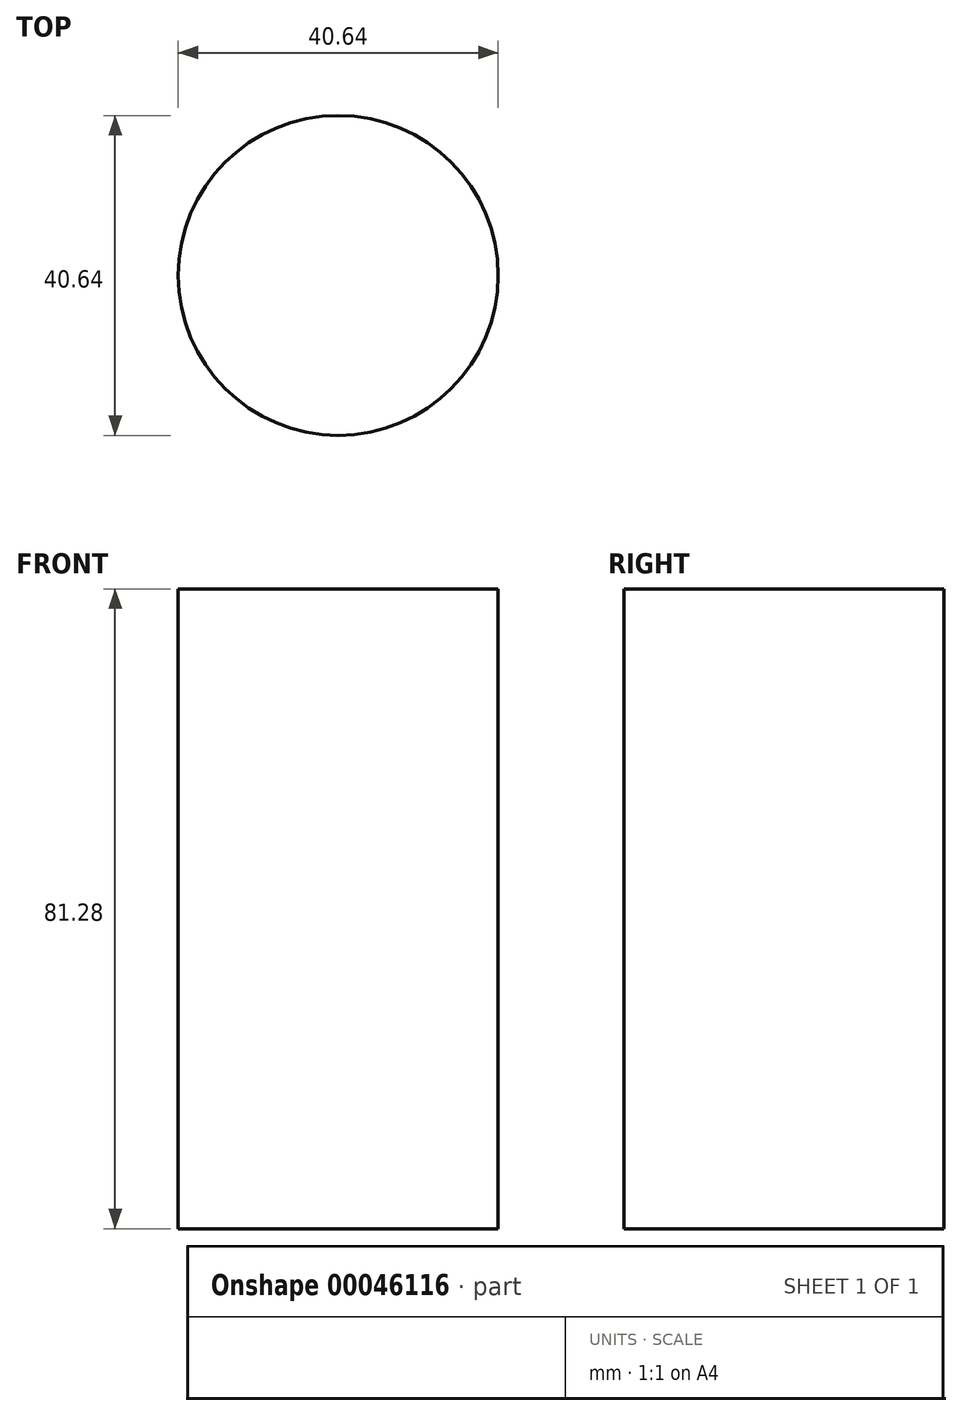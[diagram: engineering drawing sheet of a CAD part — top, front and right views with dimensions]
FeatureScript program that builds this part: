
annotation { "Feature Type Name" : "Feature", "Feature Type Description" : "" }
export const myFeature = defineFeature(function(context is Context, id is Id, definition is map)
    precondition{}
    {
        {
            var Q0;
            Q0=qCreatedBy(makeId("Top.planeOp"),FACE);
            var sketch = newSketch(context, id + "F0", { "sketchPlane" : qUnion([Q0])});
            skCircle(sketch, "E0", {"center": v(0, 0) * mm, "radius": 20.32 * mm});
            skSolve(sketch);
        }
        {
            var Q0;
            Q0 = qSketchRegion(id + "F0", true);
            extrude(context, id + "F1", {"entities" : qUnion([Q0]), "depth" : 81.28 * mm, "offsetDistance" : 25.4 * mm});
        }
        {
            var Q0;
            Q0=qCreatedBy(makeId("Front.planeOp"),FACE);
            var sketch = newSketch(context, id + "F2", { "sketchPlane" : qUnion([Q0])});
            skFitSpline(sketch, "E1", {"points": [v(-16.9, 70.92) * mm, v(-19.25, 69.07) * mm, v(-21.18, 67.72) * mm, v(-23.18, 66.68) * mm, v(-25, 65.87) * mm, v(-27.08, 65.45) * mm, v(-28.89, 65.52) * mm, v(-31.24, 66.18) * mm, v(-33.28, 67.14) * mm, v(-35.6, 68.65) * mm, v(-37.98, 70.46) * mm, v(-40.6, 72.58) * mm, v(-43.3, 74.85) * mm, v(-45.92, 76.97) * mm, v(-47.77, 78.27) * mm, v(-49.55, 79.34) * mm, v(-51.69, 80.25) * mm, v(-52.99, 80.6) * mm, v(-54.31, 80.8) * mm, v(-56.45, 80.67) * mm, v(-58.72, 79.96) * mm, v(-61.18, 78.63) * mm, v(-63.97, 76.63) * mm, v(-65.94, 74.93) * mm, v(-68.23, 72.96) * mm, v(-70.75, 70.8) * mm, v(-72.95, 68.98) * mm, v(-74.77, 67.65) * mm, v(-76.5, 66.54) * mm, v(-78.4, 65.67) * mm, v(-79.9, 65.25) * mm], "startDerivative": vector(-65.6, -51.95) * mm, "endDerivative": vector(-54.28, -13.22) * mm});
            skLineSegment(sketch, "E2", {"start": v(-16.9, 70.92) * mm, "end": v(-16.9, 68.66) * mm});
            skFitSpline(sketch, "E3", {"points": [v(-16.9, 68.66) * mm, v(-18.1, 67.65) * mm, v(-19.82, 66.42) * mm, v(-21.63, 65.25) * mm, v(-23.53, 64.2) * mm, v(-25.25, 63.55) * mm, v(-27.13, 63.23) * mm, v(-29.05, 63.26) * mm, v(-31.45, 64) * mm, v(-34.55, 65.71) * mm, v(-37.5, 67.72) * mm, v(-39.84, 69.69) * mm, v(-42.44, 71.83) * mm, v(-44.25, 73.34) * mm, v(-46.14, 74.8) * mm, v(-47.72, 75.94) * mm, v(-49.32, 76.96) * mm, v(-51.05, 77.73) * mm, v(-52.82, 78.3) * mm, v(-55.16, 78.56) * mm, v(-57.51, 78.17) * mm, v(-60.32, 76.79) * mm, v(-63.06, 74.94) * mm, v(-65.76, 72.85) * mm, v(-67.49, 71.27) * mm, v(-70.66, 68.66) * mm, v(-72.37, 67.09) * mm, v(-74.17, 65.8) * mm, v(-75.98, 64.66) * mm, v(-77.76, 63.73) * mm, v(-79.9, 62.91) * mm], "startDerivative": vector(-42.76, -36.86) * mm, "endDerivative": vector(-68.1, -24.19) * mm});
            skLineSegment(sketch, "E4", {"start": v(-79.9, 65.25) * mm, "end": v(-79.9, 62.91) * mm});
            skFitSpline(sketch, "E5", {"points": [v(-16.9, 74.77) * mm, v(-19.25, 72.92) * mm, v(-21.18, 71.57) * mm, v(-23.18, 70.53) * mm, v(-25, 69.72) * mm, v(-27.08, 69.3) * mm, v(-28.89, 69.37) * mm, v(-31.24, 70.03) * mm, v(-33.28, 71) * mm, v(-35.6, 72.5) * mm, v(-37.98, 74.3) * mm, v(-40.6, 76.43) * mm, v(-43.3, 78.7) * mm, v(-45.92, 80.82) * mm, v(-47.77, 82.12) * mm, v(-49.55, 83.19) * mm, v(-51.69, 84.1) * mm, v(-52.99, 84.45) * mm, v(-54.31, 84.65) * mm, v(-56.45, 84.52) * mm, v(-58.72, 83.8) * mm, v(-61.18, 82.48) * mm, v(-63.97, 80.48) * mm, v(-65.94, 78.78) * mm, v(-68.23, 76.81) * mm, v(-70.75, 74.66) * mm, v(-72.95, 72.82) * mm, v(-74.77, 71.5) * mm, v(-76.5, 70.4) * mm, v(-78.4, 69.52) * mm, v(-79.9, 69.1) * mm], "startDerivative": vector(-65.6, -51.95) * mm, "endDerivative": vector(-54.28, -13.22) * mm});
            skLineSegment(sketch, "E6", {"start": v(-16.9, 74.77) * mm, "end": v(-16.9, 72.51) * mm});
            skFitSpline(sketch, "E7", {"points": [v(-16.9, 72.51) * mm, v(-18.1, 71.5) * mm, v(-19.82, 70.27) * mm, v(-21.63, 69.1) * mm, v(-23.53, 68.04) * mm, v(-25.25, 67.4) * mm, v(-27.13, 67.08) * mm, v(-29.05, 67.1) * mm, v(-31.45, 67.84) * mm, v(-34.55, 69.56) * mm, v(-37.5, 71.57) * mm, v(-39.84, 73.54) * mm, v(-42.44, 75.68) * mm, v(-44.25, 77.18) * mm, v(-46.14, 78.65) * mm, v(-47.72, 79.79) * mm, v(-49.32, 80.8) * mm, v(-51.05, 81.58) * mm, v(-52.82, 82.16) * mm, v(-55.16, 82.4) * mm, v(-57.51, 82.02) * mm, v(-60.32, 80.63) * mm, v(-63.06, 78.78) * mm, v(-65.76, 76.7) * mm, v(-67.49, 75.12) * mm, v(-70.66, 72.51) * mm, v(-72.37, 70.94) * mm, v(-74.17, 69.65) * mm, v(-75.98, 68.5) * mm, v(-77.76, 67.58) * mm, v(-79.9, 66.76) * mm], "startDerivative": vector(-42.76, -36.86) * mm, "endDerivative": vector(-68.1, -24.19) * mm});
            skLineSegment(sketch, "E8", {"start": v(-79.9, 69.1) * mm, "end": v(-79.9, 66.76) * mm});
            skFitSpline(sketch, "E9", {"points": [v(-16.9, 78.33) * mm, v(-19.25, 76.47) * mm, v(-21.18, 75.12) * mm, v(-23.18, 74.08) * mm, v(-25, 73.27) * mm, v(-27.08, 72.85) * mm, v(-28.89, 72.93) * mm, v(-31.24, 73.58) * mm, v(-33.28, 74.55) * mm, v(-35.6, 76.05) * mm, v(-37.98, 77.86) * mm, v(-40.6, 79.98) * mm, v(-43.3, 82.25) * mm, v(-45.92, 84.38) * mm, v(-47.77, 85.67) * mm, v(-49.55, 86.74) * mm, v(-51.69, 87.65) * mm, v(-52.99, 88) * mm, v(-54.31, 88.2) * mm, v(-56.45, 88.07) * mm, v(-58.72, 87.36) * mm, v(-61.18, 86.03) * mm, v(-63.97, 84.03) * mm, v(-65.94, 82.34) * mm, v(-68.23, 80.37) * mm, v(-70.75, 78.21) * mm, v(-72.95, 76.38) * mm, v(-74.77, 75.05) * mm, v(-76.5, 73.95) * mm, v(-78.4, 73.07) * mm, v(-79.9, 72.65) * mm], "startDerivative": vector(-65.6, -51.95) * mm, "endDerivative": vector(-54.28, -13.22) * mm});
            skLineSegment(sketch, "E10", {"start": v(-16.9, 78.33) * mm, "end": v(-16.9, 76.07) * mm});
            skFitSpline(sketch, "E11", {"points": [v(-16.9, 76.07) * mm, v(-18.1, 75.06) * mm, v(-19.82, 73.82) * mm, v(-21.63, 72.65) * mm, v(-23.53, 71.6) * mm, v(-25.25, 70.96) * mm, v(-27.13, 70.64) * mm, v(-29.05, 70.66) * mm, v(-31.45, 71.4) * mm, v(-34.55, 73.11) * mm, v(-37.5, 75.12) * mm, v(-39.84, 77.1) * mm, v(-42.44, 79.24) * mm, v(-44.25, 80.74) * mm, v(-46.14, 82.2) * mm, v(-47.72, 83.34) * mm, v(-49.32, 84.36) * mm, v(-51.05, 85.13) * mm, v(-52.82, 85.71) * mm, v(-55.16, 85.96) * mm, v(-57.51, 85.58) * mm, v(-60.32, 84.19) * mm, v(-63.06, 82.34) * mm, v(-65.76, 80.26) * mm, v(-67.49, 78.68) * mm, v(-70.66, 76.07) * mm, v(-72.37, 74.49) * mm, v(-74.17, 73.2) * mm, v(-75.98, 72.06) * mm, v(-77.76, 71.13) * mm, v(-79.9, 70.32) * mm], "startDerivative": vector(-42.76, -36.86) * mm, "endDerivative": vector(-68.1, -24.19) * mm});
            skLineSegment(sketch, "E12", {"start": v(-79.9, 72.65) * mm, "end": v(-79.9, 70.32) * mm});
            skFitSpline(sketch, "E13", {"points": [v(-16.9, 81.98) * mm, v(-19.25, 80.13) * mm, v(-21.18, 78.78) * mm, v(-23.18, 77.74) * mm, v(-25, 76.93) * mm, v(-27.08, 76.5) * mm, v(-28.89, 76.58) * mm, v(-31.24, 77.24) * mm, v(-33.28, 78.2) * mm, v(-35.6, 79.7) * mm, v(-37.98, 81.52) * mm, v(-40.6, 83.64) * mm, v(-43.3, 85.9) * mm, v(-45.92, 88.03) * mm, v(-47.77, 89.33) * mm, v(-49.55, 90.4) * mm, v(-51.69, 91.3) * mm, v(-52.99, 91.66) * mm, v(-54.31, 91.86) * mm, v(-56.45, 91.73) * mm, v(-58.72, 91.01) * mm, v(-61.18, 89.69) * mm, v(-63.97, 87.69) * mm, v(-65.94, 86) * mm, v(-68.23, 84.02) * mm, v(-70.75, 81.87) * mm, v(-72.95, 80.03) * mm, v(-74.77, 78.7) * mm, v(-76.5, 77.6) * mm, v(-78.4, 76.73) * mm, v(-79.9, 76.3) * mm], "startDerivative": vector(-65.6, -51.95) * mm, "endDerivative": vector(-54.28, -13.22) * mm});
            skLineSegment(sketch, "E14", {"start": v(-16.9, 81.71) * mm, "end": v(-16.9, 79.72) * mm});
            skFitSpline(sketch, "E15", {"points": [v(-16.9, 79.72) * mm, v(-18.1, 78.71) * mm, v(-19.82, 77.48) * mm, v(-21.63, 76.3) * mm, v(-23.53, 75.25) * mm, v(-25.25, 74.61) * mm, v(-27.13, 74.3) * mm, v(-29.05, 74.32) * mm, v(-31.45, 75.05) * mm, v(-34.55, 76.77) * mm, v(-37.5, 78.78) * mm, v(-39.84, 80.75) * mm, v(-42.44, 82.9) * mm, v(-44.25, 84.4) * mm, v(-46.14, 85.86) * mm, v(-47.72, 87) * mm, v(-49.32, 88.02) * mm, v(-51.05, 88.79) * mm, v(-52.82, 89.37) * mm, v(-55.16, 89.62) * mm, v(-57.51, 89.23) * mm, v(-60.32, 87.84) * mm, v(-63.06, 86) * mm, v(-65.76, 83.91) * mm, v(-67.49, 82.33) * mm, v(-70.66, 79.72) * mm, v(-72.37, 78.15) * mm, v(-74.17, 76.87) * mm, v(-75.98, 75.72) * mm, v(-77.76, 74.79) * mm, v(-79.9, 73.97) * mm], "startDerivative": vector(-42.76, -36.86) * mm, "endDerivative": vector(-68.1, -24.19) * mm});
            skLineSegment(sketch, "E16", {"start": v(-79.9, 76.3) * mm, "end": v(-79.9, 73.97) * mm});
            skFitSpline(sketch, "E17", {"points": [v(-16.9, 85.8) * mm, v(-19.25, 83.95) * mm, v(-21.18, 82.6) * mm, v(-23.18, 81.56) * mm, v(-25, 80.75) * mm, v(-27.08, 80.33) * mm, v(-28.89, 80.4) * mm, v(-31.24, 81.06) * mm, v(-33.28, 82.03) * mm, v(-35.6, 83.53) * mm, v(-37.98, 85.34) * mm, v(-40.6, 87.46) * mm, v(-43.3, 89.73) * mm, v(-45.92, 91.86) * mm, v(-47.77, 93.15) * mm, v(-49.55, 94.22) * mm, v(-51.69, 95.13) * mm, v(-52.99, 95.49) * mm, v(-54.31, 95.68) * mm, v(-56.45, 95.55) * mm, v(-58.72, 94.84) * mm, v(-61.18, 93.5) * mm, v(-63.97, 91.51) * mm, v(-65.94, 89.82) * mm, v(-68.23, 87.85) * mm, v(-70.75, 85.7) * mm, v(-72.95, 83.86) * mm, v(-74.77, 82.53) * mm, v(-76.5, 81.43) * mm, v(-78.4, 80.55) * mm, v(-79.9, 80.13) * mm], "startDerivative": vector(-65.6, -51.95) * mm, "endDerivative": vector(-54.28, -13.22) * mm});
            skLineSegment(sketch, "E18", {"start": v(-16.9, 85.8) * mm, "end": v(-16.9, 83.55) * mm});
            skFitSpline(sketch, "E19", {"points": [v(-16.9, 83.55) * mm, v(-18.1, 82.54) * mm, v(-19.82, 81.3) * mm, v(-21.63, 80.13) * mm, v(-23.53, 79.08) * mm, v(-25.25, 78.44) * mm, v(-27.13, 78.11) * mm, v(-29.05, 78.14) * mm, v(-31.45, 78.88) * mm, v(-34.55, 80.6) * mm, v(-37.5, 82.6) * mm, v(-39.84, 84.57) * mm, v(-42.44, 86.72) * mm, v(-44.25, 88.22) * mm, v(-46.14, 89.68) * mm, v(-47.72, 90.82) * mm, v(-49.32, 91.84) * mm, v(-51.05, 92.61) * mm, v(-52.82, 93.19) * mm, v(-55.16, 93.44) * mm, v(-57.51, 93.06) * mm, v(-60.32, 91.67) * mm, v(-63.06, 89.82) * mm, v(-65.76, 87.74) * mm, v(-67.49, 86.15) * mm, v(-70.66, 83.55) * mm, v(-72.37, 81.97) * mm, v(-74.17, 80.69) * mm, v(-75.98, 79.54) * mm, v(-77.76, 78.61) * mm, v(-79.9, 77.8) * mm], "startDerivative": vector(-42.76, -36.86) * mm, "endDerivative": vector(-68.1, -24.19) * mm});
            skLineSegment(sketch, "E20", {"start": v(-79.9, 80.13) * mm, "end": v(-79.9, 77.8) * mm});
            skFitSpline(sketch, "E21", {"points": [v(-16.9, 67.25) * mm, v(-19.25, 65.4) * mm, v(-21.18, 64.05) * mm, v(-23.18, 63) * mm, v(-25, 62.2) * mm, v(-27.08, 61.78) * mm, v(-28.89, 61.85) * mm, v(-31.24, 62.5) * mm, v(-33.28, 63.47) * mm, v(-35.6, 64.97) * mm, v(-37.98, 66.79) * mm, v(-40.6, 68.9) * mm, v(-43.3, 71.18) * mm, v(-45.92, 73.3) * mm, v(-47.77, 74.6) * mm, v(-49.55, 75.67) * mm, v(-51.69, 76.58) * mm, v(-52.99, 76.93) * mm, v(-54.31, 77.13) * mm, v(-56.45, 77) * mm, v(-58.72, 76.28) * mm, v(-61.18, 74.96) * mm, v(-63.97, 72.96) * mm, v(-65.94, 71.26) * mm, v(-68.23, 69.3) * mm, v(-70.75, 67.14) * mm, v(-72.95, 65.3) * mm, v(-74.77, 63.97) * mm, v(-76.5, 62.87) * mm, v(-78.4, 62) * mm, v(-79.9, 61.58) * mm], "startDerivative": vector(-65.6, -51.95) * mm, "endDerivative": vector(-54.28, -13.22) * mm});
            skLineSegment(sketch, "E22", {"start": v(-16.9, 67.25) * mm, "end": v(-16.9, 65) * mm});
            skFitSpline(sketch, "E23", {"points": [v(-16.9, 65) * mm, v(-18.1, 63.98) * mm, v(-19.82, 62.75) * mm, v(-21.63, 61.58) * mm, v(-23.53, 60.52) * mm, v(-25.25, 59.88) * mm, v(-27.13, 59.56) * mm, v(-29.05, 59.59) * mm, v(-31.45, 60.32) * mm, v(-34.55, 62.04) * mm, v(-37.5, 64.05) * mm, v(-39.84, 66.02) * mm, v(-42.44, 68.16) * mm, v(-44.25, 69.66) * mm, v(-46.14, 71.13) * mm, v(-47.72, 72.27) * mm, v(-49.32, 73.29) * mm, v(-51.05, 74.06) * mm, v(-52.82, 74.64) * mm, v(-55.16, 74.89) * mm, v(-57.51, 74.5) * mm, v(-60.32, 73.11) * mm, v(-63.06, 71.26) * mm, v(-65.76, 69.18) * mm, v(-67.49, 67.6) * mm, v(-70.66, 65) * mm, v(-72.37, 63.42) * mm, v(-74.17, 62.13) * mm, v(-75.98, 60.98) * mm, v(-77.76, 60.06) * mm, v(-79.9, 59.24) * mm], "startDerivative": vector(-42.76, -36.86) * mm, "endDerivative": vector(-68.1, -24.19) * mm});
            skLineSegment(sketch, "E24", {"start": v(-79.9, 61.58) * mm, "end": v(-79.9, 59.24) * mm});
            skFitSpline(sketch, "E25", {"points": [v(-16.9, 63.52) * mm, v(-19.25, 61.66) * mm, v(-21.18, 60.32) * mm, v(-23.18, 59.28) * mm, v(-25, 58.47) * mm, v(-27.08, 58.04) * mm, v(-28.89, 58.12) * mm, v(-31.24, 58.77) * mm, v(-33.28, 59.74) * mm, v(-35.6, 61.24) * mm, v(-37.98, 63.05) * mm, v(-40.6, 65.17) * mm, v(-43.3, 67.45) * mm, v(-45.92, 69.57) * mm, v(-47.77, 70.87) * mm, v(-49.55, 71.93) * mm, v(-51.69, 72.84) * mm, v(-52.99, 73.2) * mm, v(-54.31, 73.4) * mm, v(-56.45, 73.26) * mm, v(-58.72, 72.55) * mm, v(-61.18, 71.22) * mm, v(-63.97, 69.22) * mm, v(-65.94, 67.53) * mm, v(-68.23, 65.56) * mm, v(-70.75, 63.4) * mm, v(-72.95, 61.57) * mm, v(-74.77, 60.24) * mm, v(-76.5, 59.14) * mm, v(-78.4, 58.26) * mm, v(-79.9, 57.84) * mm], "startDerivative": vector(-65.6, -51.95) * mm, "endDerivative": vector(-54.28, -13.22) * mm});
            skLineSegment(sketch, "E26", {"start": v(-16.9, 63.52) * mm, "end": v(-16.9, 61.26) * mm});
            skFitSpline(sketch, "E27", {"points": [v(-16.9, 61.26) * mm, v(-18.1, 60.25) * mm, v(-19.82, 59.01) * mm, v(-21.63, 57.84) * mm, v(-23.53, 56.79) * mm, v(-25.25, 56.15) * mm, v(-27.13, 55.83) * mm, v(-29.05, 55.85) * mm, v(-31.45, 56.59) * mm, v(-34.55, 58.3) * mm, v(-37.5, 60.32) * mm, v(-39.84, 62.28) * mm, v(-42.44, 64.43) * mm, v(-44.25, 65.93) * mm, v(-46.14, 67.4) * mm, v(-47.72, 68.53) * mm, v(-49.32, 69.55) * mm, v(-51.05, 70.32) * mm, v(-52.82, 70.9) * mm, v(-55.16, 71.15) * mm, v(-57.51, 70.77) * mm, v(-60.32, 69.38) * mm, v(-63.06, 67.53) * mm, v(-65.76, 65.45) * mm, v(-67.49, 63.87) * mm, v(-70.66, 61.26) * mm, v(-72.37, 59.68) * mm, v(-74.17, 58.4) * mm, v(-75.98, 57.25) * mm, v(-77.76, 56.32) * mm, v(-79.9, 55.5) * mm], "startDerivative": vector(-42.76, -36.86) * mm, "endDerivative": vector(-68.1, -24.19) * mm});
            skLineSegment(sketch, "E28", {"start": v(-79.9, 57.84) * mm, "end": v(-79.9, 55.5) * mm});
            skFitSpline(sketch, "E29", {"points": [v(-16.9, 60.09) * mm, v(-19.25, 58.23) * mm, v(-21.18, 56.88) * mm, v(-23.18, 55.84) * mm, v(-25, 55.03) * mm, v(-27.08, 54.6) * mm, v(-28.89, 54.69) * mm, v(-31.24, 55.34) * mm, v(-33.28, 56.3) * mm, v(-35.6, 57.8) * mm, v(-37.98, 59.62) * mm, v(-40.6, 61.74) * mm, v(-43.3, 64.01) * mm, v(-45.92, 66.14) * mm, v(-47.77, 67.43) * mm, v(-49.55, 68.5) * mm, v(-51.69, 69.4) * mm, v(-52.99, 69.77) * mm, v(-54.31, 69.96) * mm, v(-56.45, 69.83) * mm, v(-58.72, 69.12) * mm, v(-61.18, 67.79) * mm, v(-63.97, 65.8) * mm, v(-65.94, 64.1) * mm, v(-68.23, 62.12) * mm, v(-70.75, 59.97) * mm, v(-72.95, 58.14) * mm, v(-74.77, 56.8) * mm, v(-76.5, 55.7) * mm, v(-78.4, 54.83) * mm, v(-79.9, 54.4) * mm], "startDerivative": vector(-65.6, -51.95) * mm, "endDerivative": vector(-54.28, -13.22) * mm});
            skLineSegment(sketch, "E30", {"start": v(-16.9, 60.09) * mm, "end": v(-16.9, 57.82) * mm});
            skFitSpline(sketch, "E31", {"points": [v(-16.9, 57.82) * mm, v(-18.1, 56.82) * mm, v(-19.82, 55.58) * mm, v(-21.63, 54.41) * mm, v(-23.53, 53.36) * mm, v(-25.25, 52.71) * mm, v(-27.13, 52.4) * mm, v(-29.05, 52.42) * mm, v(-31.45, 53.16) * mm, v(-34.55, 54.87) * mm, v(-37.5, 56.88) * mm, v(-39.84, 58.85) * mm, v(-42.44, 61) * mm, v(-44.25, 62.5) * mm, v(-46.14, 63.96) * mm, v(-47.72, 65.1) * mm, v(-49.32, 66.12) * mm, v(-51.05, 66.9) * mm, v(-52.82, 67.47) * mm, v(-55.16, 67.72) * mm, v(-57.51, 67.34) * mm, v(-60.32, 65.95) * mm, v(-63.06, 64.1) * mm, v(-65.76, 62.02) * mm, v(-67.49, 60.43) * mm, v(-70.66, 57.82) * mm, v(-72.37, 56.25) * mm, v(-74.17, 54.97) * mm, v(-75.98, 53.82) * mm, v(-77.76, 52.9) * mm, v(-79.9, 52.07) * mm], "startDerivative": vector(-42.76, -36.86) * mm, "endDerivative": vector(-68.1, -24.19) * mm});
            skLineSegment(sketch, "E32", {"start": v(-79.9, 54.4) * mm, "end": v(-79.9, 52.07) * mm});
            skFitSpline(sketch, "E33", {"points": [v(-16.9, 56.45) * mm, v(-19.25, 54.6) * mm, v(-21.18, 53.25) * mm, v(-23.18, 52.21) * mm, v(-25, 51.4) * mm, v(-27.08, 50.98) * mm, v(-28.89, 51.05) * mm, v(-31.24, 51.7) * mm, v(-33.28, 52.67) * mm, v(-35.6, 54.18) * mm, v(-37.98, 55.99) * mm, v(-40.6, 58.1) * mm, v(-43.3, 60.38) * mm, v(-45.92, 62.5) * mm, v(-47.77, 63.8) * mm, v(-49.55, 64.87) * mm, v(-51.69, 65.78) * mm, v(-52.99, 66.13) * mm, v(-54.31, 66.33) * mm, v(-56.45, 66.2) * mm, v(-58.72, 65.49) * mm, v(-61.18, 64.16) * mm, v(-63.97, 62.16) * mm, v(-65.94, 60.46) * mm, v(-68.23, 58.5) * mm, v(-70.75, 56.34) * mm, v(-72.95, 54.5) * mm, v(-74.77, 53.18) * mm, v(-76.5, 52.07) * mm, v(-78.4, 51.2) * mm, v(-79.9, 50.78) * mm], "startDerivative": vector(-65.6, -51.95) * mm, "endDerivative": vector(-54.28, -13.22) * mm});
            skLineSegment(sketch, "E34", {"start": v(-16.9, 56.45) * mm, "end": v(-16.9, 54.2) * mm});
            skFitSpline(sketch, "E35", {"points": [v(-16.9, 54.2) * mm, v(-18.1, 53.18) * mm, v(-19.82, 51.95) * mm, v(-21.63, 50.78) * mm, v(-23.53, 49.72) * mm, v(-25.25, 49.08) * mm, v(-27.13, 48.76) * mm, v(-29.05, 48.79) * mm, v(-31.45, 49.52) * mm, v(-34.55, 51.24) * mm, v(-37.5, 53.25) * mm, v(-39.84, 55.22) * mm, v(-42.44, 57.36) * mm, v(-44.25, 58.87) * mm, v(-46.14, 60.33) * mm, v(-47.72, 61.47) * mm, v(-49.32, 62.49) * mm, v(-51.05, 63.26) * mm, v(-52.82, 63.84) * mm, v(-55.16, 64.09) * mm, v(-57.51, 63.7) * mm, v(-60.32, 62.32) * mm, v(-63.06, 60.47) * mm, v(-65.76, 58.38) * mm, v(-67.49, 56.8) * mm, v(-70.66, 54.2) * mm, v(-72.37, 52.62) * mm, v(-74.17, 51.34) * mm, v(-75.98, 50.19) * mm, v(-77.76, 49.26) * mm, v(-79.9, 48.44) * mm], "startDerivative": vector(-42.76, -36.86) * mm, "endDerivative": vector(-68.1, -24.19) * mm});
            skLineSegment(sketch, "E36", {"start": v(-79.9, 50.78) * mm, "end": v(-79.9, 48.44) * mm});
            skFitSpline(sketch, "E37", {"points": [v(-16.9, 52.7) * mm, v(-19.25, 50.84) * mm, v(-21.18, 49.5) * mm, v(-23.18, 48.45) * mm, v(-25, 47.64) * mm, v(-27.08, 47.22) * mm, v(-28.89, 47.3) * mm, v(-31.24, 47.95) * mm, v(-33.28, 48.91) * mm, v(-35.6, 50.42) * mm, v(-37.98, 52.23) * mm, v(-40.6, 54.35) * mm, v(-43.3, 56.62) * mm, v(-45.92, 58.74) * mm, v(-47.77, 60.04) * mm, v(-49.55, 61.11) * mm, v(-51.69, 62.02) * mm, v(-52.99, 62.37) * mm, v(-54.31, 62.57) * mm, v(-56.45, 62.44) * mm, v(-58.72, 61.73) * mm, v(-61.18, 60.4) * mm, v(-63.97, 58.4) * mm, v(-65.94, 56.7) * mm, v(-68.23, 54.73) * mm, v(-70.75, 52.58) * mm, v(-72.95, 50.75) * mm, v(-74.77, 49.42) * mm, v(-76.5, 48.31) * mm, v(-78.4, 47.44) * mm, v(-79.9, 47.02) * mm], "startDerivative": vector(-65.6, -51.95) * mm, "endDerivative": vector(-54.28, -13.22) * mm});
            skLineSegment(sketch, "E38", {"start": v(-16.9, 52.7) * mm, "end": v(-16.9, 50.43) * mm});
            skFitSpline(sketch, "E39", {"points": [v(-16.9, 50.43) * mm, v(-18.1, 49.43) * mm, v(-19.82, 48.19) * mm, v(-21.63, 47.02) * mm, v(-23.53, 45.97) * mm, v(-25.25, 45.32) * mm, v(-27.13, 45) * mm, v(-29.05, 45.03) * mm, v(-31.45, 45.76) * mm, v(-34.55, 47.48) * mm, v(-37.5, 49.5) * mm, v(-39.84, 51.46) * mm, v(-42.44, 53.6) * mm, v(-44.25, 55.1) * mm, v(-46.14, 56.57) * mm, v(-47.72, 57.7) * mm, v(-49.32, 58.73) * mm, v(-51.05, 59.5) * mm, v(-52.82, 60.08) * mm, v(-55.16, 60.33) * mm, v(-57.51, 59.94) * mm, v(-60.32, 58.56) * mm, v(-63.06, 56.7) * mm, v(-65.76, 54.63) * mm, v(-67.49, 53.04) * mm, v(-70.66, 50.43) * mm, v(-72.37, 48.86) * mm, v(-74.17, 47.58) * mm, v(-75.98, 46.43) * mm, v(-77.76, 45.5) * mm, v(-79.9, 44.68) * mm], "startDerivative": vector(-42.76, -36.86) * mm, "endDerivative": vector(-68.1, -24.19) * mm});
            skLineSegment(sketch, "E40", {"start": v(-79.9, 47.02) * mm, "end": v(-79.9, 44.68) * mm});
            skFitSpline(sketch, "E41", {"points": [v(-16.9, 49.16) * mm, v(-19.25, 47.3) * mm, v(-21.18, 45.96) * mm, v(-23.18, 44.92) * mm, v(-25, 44.11) * mm, v(-27.08, 43.69) * mm, v(-28.89, 43.76) * mm, v(-31.24, 44.42) * mm, v(-33.28, 45.38) * mm, v(-35.6, 46.89) * mm, v(-37.98, 48.7) * mm, v(-40.6, 50.82) * mm, v(-43.3, 53.1) * mm, v(-45.92, 55.21) * mm, v(-47.77, 56.51) * mm, v(-49.55, 57.58) * mm, v(-51.69, 58.49) * mm, v(-52.99, 58.84) * mm, v(-54.31, 59.04) * mm, v(-56.45, 58.9) * mm, v(-58.72, 58.2) * mm, v(-61.18, 56.87) * mm, v(-63.97, 54.87) * mm, v(-65.94, 53.17) * mm, v(-68.23, 51.2) * mm, v(-70.75, 49.05) * mm, v(-72.95, 47.22) * mm, v(-74.77, 45.89) * mm, v(-76.5, 44.78) * mm, v(-78.4, 43.9) * mm, v(-79.9, 43.49) * mm], "startDerivative": vector(-65.6, -51.95) * mm, "endDerivative": vector(-54.28, -13.22) * mm});
            skLineSegment(sketch, "E42", {"start": v(-16.9, 49.16) * mm, "end": v(-16.9, 46.9) * mm});
            skFitSpline(sketch, "E43", {"points": [v(-16.9, 46.9) * mm, v(-18.1, 45.9) * mm, v(-19.82, 44.66) * mm, v(-21.63, 43.49) * mm, v(-23.53, 42.43) * mm, v(-25.25, 41.8) * mm, v(-27.13, 41.47) * mm, v(-29.05, 41.5) * mm, v(-31.45, 42.23) * mm, v(-34.55, 43.95) * mm, v(-37.5, 45.96) * mm, v(-39.84, 47.93) * mm, v(-42.44, 50.07) * mm, v(-44.25, 51.58) * mm, v(-46.14, 53.04) * mm, v(-47.72, 54.18) * mm, v(-49.32, 55.2) * mm, v(-51.05, 55.97) * mm, v(-52.82, 56.55) * mm, v(-55.16, 56.8) * mm, v(-57.51, 56.41) * mm, v(-60.32, 55.03) * mm, v(-63.06, 53.18) * mm, v(-65.76, 51.1) * mm, v(-67.49, 49.51) * mm, v(-70.66, 46.9) * mm, v(-72.37, 45.33) * mm, v(-74.17, 44.05) * mm, v(-75.98, 42.9) * mm, v(-77.76, 41.97) * mm, v(-79.9, 41.15) * mm], "startDerivative": vector(-42.76, -36.86) * mm, "endDerivative": vector(-68.1, -24.19) * mm});
            skLineSegment(sketch, "E44", {"start": v(-79.9, 43.49) * mm, "end": v(-79.9, 41.15) * mm});
            skFitSpline(sketch, "E45", {"points": [v(-16.9, 45.4) * mm, v(-19.25, 43.55) * mm, v(-21.18, 42.2) * mm, v(-23.18, 41.16) * mm, v(-25, 40.35) * mm, v(-27.08, 39.92) * mm, v(-28.89, 40) * mm, v(-31.24, 40.66) * mm, v(-33.28, 41.62) * mm, v(-35.6, 43.12) * mm, v(-37.98, 44.93) * mm, v(-40.6, 47.05) * mm, v(-43.3, 49.33) * mm, v(-45.92, 51.45) * mm, v(-47.77, 52.75) * mm, v(-49.55, 53.82) * mm, v(-51.69, 54.72) * mm, v(-52.99, 55.08) * mm, v(-54.31, 55.28) * mm, v(-56.45, 55.15) * mm, v(-58.72, 54.43) * mm, v(-61.18, 53.1) * mm, v(-63.97, 51.1) * mm, v(-65.94, 49.41) * mm, v(-68.23, 47.44) * mm, v(-70.75, 45.29) * mm, v(-72.95, 43.45) * mm, v(-74.77, 42.12) * mm, v(-76.5, 41.02) * mm, v(-78.4, 40.15) * mm, v(-79.9, 39.72) * mm], "startDerivative": vector(-65.6, -51.95) * mm, "endDerivative": vector(-54.28, -13.22) * mm});
            skLineSegment(sketch, "E46", {"start": v(-16.9, 45.4) * mm, "end": v(-16.9, 43.14) * mm});
            skFitSpline(sketch, "E47", {"points": [v(-16.9, 43.14) * mm, v(-18.1, 42.13) * mm, v(-19.82, 40.9) * mm, v(-21.63, 39.73) * mm, v(-23.53, 38.67) * mm, v(-25.25, 38.03) * mm, v(-27.13, 37.7) * mm, v(-29.05, 37.74) * mm, v(-31.45, 38.47) * mm, v(-34.55, 40.19) * mm, v(-37.5, 42.2) * mm, v(-39.84, 44.17) * mm, v(-42.44, 46.31) * mm, v(-44.25, 47.81) * mm, v(-46.14, 49.28) * mm, v(-47.72, 50.41) * mm, v(-49.32, 51.44) * mm, v(-51.05, 52.2) * mm, v(-52.82, 52.78) * mm, v(-55.16, 53.04) * mm, v(-57.51, 52.65) * mm, v(-60.32, 51.26) * mm, v(-63.06, 49.41) * mm, v(-65.76, 47.33) * mm, v(-67.49, 45.75) * mm, v(-70.66, 43.14) * mm, v(-72.37, 41.56) * mm, v(-74.17, 40.28) * mm, v(-75.98, 39.13) * mm, v(-77.76, 38.2) * mm, v(-79.9, 37.39) * mm], "startDerivative": vector(-42.76, -36.86) * mm, "endDerivative": vector(-68.1, -24.19) * mm});
            skLineSegment(sketch, "E48", {"start": v(-79.9, 39.72) * mm, "end": v(-79.9, 37.39) * mm});
            skFitSpline(sketch, "E49", {"points": [v(-16.9, 41.6) * mm, v(-19.25, 39.74) * mm, v(-21.18, 38.39) * mm, v(-23.18, 37.35) * mm, v(-25, 36.54) * mm, v(-27.08, 36.11) * mm, v(-28.89, 36.2) * mm, v(-31.24, 36.85) * mm, v(-33.28, 37.81) * mm, v(-35.6, 39.31) * mm, v(-37.98, 41.12) * mm, v(-40.6, 43.24) * mm, v(-43.3, 45.52) * mm, v(-45.92, 47.64) * mm, v(-47.77, 48.94) * mm, v(-49.55, 50) * mm, v(-51.69, 50.91) * mm, v(-52.99, 51.27) * mm, v(-54.31, 51.47) * mm, v(-56.45, 51.34) * mm, v(-58.72, 50.62) * mm, v(-61.18, 49.3) * mm, v(-63.97, 47.3) * mm, v(-65.94, 45.6) * mm, v(-68.23, 43.63) * mm, v(-70.75, 41.48) * mm, v(-72.95, 39.64) * mm, v(-74.77, 38.31) * mm, v(-76.5, 37.21) * mm, v(-78.4, 36.34) * mm, v(-79.9, 35.91) * mm], "startDerivative": vector(-65.6, -51.95) * mm, "endDerivative": vector(-54.28, -13.22) * mm});
            skLineSegment(sketch, "E50", {"start": v(-16.9, 41.6) * mm, "end": v(-16.9, 39.33) * mm});
            skFitSpline(sketch, "E51", {"points": [v(-16.9, 39.33) * mm, v(-18.1, 38.32) * mm, v(-19.82, 37.08) * mm, v(-21.63, 35.92) * mm, v(-23.53, 34.86) * mm, v(-25.25, 34.22) * mm, v(-27.13, 33.9) * mm, v(-29.05, 33.93) * mm, v(-31.45, 34.66) * mm, v(-34.55, 36.38) * mm, v(-37.5, 38.39) * mm, v(-39.84, 40.36) * mm, v(-42.44, 42.5) * mm, v(-44.25, 44) * mm, v(-46.14, 45.47) * mm, v(-47.72, 46.6) * mm, v(-49.32, 47.63) * mm, v(-51.05, 48.4) * mm, v(-52.82, 48.97) * mm, v(-55.16, 49.23) * mm, v(-57.51, 48.84) * mm, v(-60.32, 47.45) * mm, v(-63.06, 45.6) * mm, v(-65.76, 43.52) * mm, v(-67.49, 41.94) * mm, v(-70.66, 39.33) * mm, v(-72.37, 37.75) * mm, v(-74.17, 36.47) * mm, v(-75.98, 35.32) * mm, v(-77.76, 34.4) * mm, v(-79.9, 33.58) * mm], "startDerivative": vector(-42.76, -36.86) * mm, "endDerivative": vector(-68.1, -24.19) * mm});
            skLineSegment(sketch, "E52", {"start": v(-79.9, 35.91) * mm, "end": v(-79.9, 33.58) * mm});
            skFitSpline(sketch, "E53", {"points": [v(-16.9, 37.83) * mm, v(-19.25, 35.98) * mm, v(-21.18, 34.63) * mm, v(-23.18, 33.59) * mm, v(-25, 32.78) * mm, v(-27.08, 32.36) * mm, v(-28.89, 32.43) * mm, v(-31.24, 33.09) * mm, v(-33.28, 34.05) * mm, v(-35.6, 35.55) * mm, v(-37.98, 37.37) * mm, v(-40.6, 39.49) * mm, v(-43.3, 41.76) * mm, v(-45.92, 43.88) * mm, v(-47.77, 45.18) * mm, v(-49.55, 46.25) * mm, v(-51.69, 47.16) * mm, v(-52.99, 47.51) * mm, v(-54.31, 47.7) * mm, v(-56.45, 47.58) * mm, v(-58.72, 46.86) * mm, v(-61.18, 45.54) * mm, v(-63.97, 43.54) * mm, v(-65.94, 41.84) * mm, v(-68.23, 39.87) * mm, v(-70.75, 37.72) * mm, v(-72.95, 35.88) * mm, v(-74.77, 34.55) * mm, v(-76.5, 33.45) * mm, v(-78.4, 32.58) * mm, v(-79.9, 32.16) * mm], "startDerivative": vector(-65.6, -51.95) * mm, "endDerivative": vector(-54.28, -13.22) * mm});
            skLineSegment(sketch, "E54", {"start": v(-16.9, 37.83) * mm, "end": v(-16.9, 35.57) * mm});
            skFitSpline(sketch, "E55", {"points": [v(-16.9, 35.57) * mm, v(-18.1, 34.56) * mm, v(-19.82, 33.33) * mm, v(-21.63, 32.16) * mm, v(-23.53, 31.1) * mm, v(-25.25, 30.46) * mm, v(-27.13, 30.14) * mm, v(-29.05, 30.17) * mm, v(-31.45, 30.9) * mm, v(-34.55, 32.62) * mm, v(-37.5, 34.63) * mm, v(-39.84, 36.6) * mm, v(-42.44, 38.74) * mm, v(-44.25, 40.24) * mm, v(-46.14, 41.7) * mm, v(-47.72, 42.85) * mm, v(-49.32, 43.87) * mm, v(-51.05, 44.64) * mm, v(-52.82, 45.22) * mm, v(-55.16, 45.47) * mm, v(-57.51, 45.08) * mm, v(-60.32, 43.7) * mm, v(-63.06, 41.84) * mm, v(-65.76, 39.76) * mm, v(-67.49, 38.18) * mm, v(-70.66, 35.57) * mm, v(-72.37, 34) * mm, v(-74.17, 32.71) * mm, v(-75.98, 31.56) * mm, v(-77.76, 30.64) * mm, v(-79.9, 29.82) * mm], "startDerivative": vector(-42.76, -36.86) * mm, "endDerivative": vector(-68.1, -24.19) * mm});
            skLineSegment(sketch, "E56", {"start": v(-79.9, 32.16) * mm, "end": v(-79.9, 29.82) * mm});
            skFitSpline(sketch, "E57", {"points": [v(-16.9, 34.22) * mm, v(-19.25, 32.37) * mm, v(-21.18, 31.02) * mm, v(-23.18, 29.98) * mm, v(-25, 29.17) * mm, v(-27.08, 28.75) * mm, v(-28.89, 28.82) * mm, v(-31.24, 29.48) * mm, v(-33.28, 30.44) * mm, v(-35.6, 31.95) * mm, v(-37.98, 33.76) * mm, v(-40.6, 35.88) * mm, v(-43.3, 38.15) * mm, v(-45.92, 40.27) * mm, v(-47.77, 41.57) * mm, v(-49.55, 42.64) * mm, v(-51.69, 43.55) * mm, v(-52.99, 43.9) * mm, v(-54.31, 44.1) * mm, v(-56.45, 43.97) * mm, v(-58.72, 43.25) * mm, v(-61.18, 41.93) * mm, v(-63.97, 39.93) * mm, v(-65.94, 38.23) * mm, v(-68.23, 36.26) * mm, v(-70.75, 34.1) * mm, v(-72.95, 32.27) * mm, v(-74.77, 30.94) * mm, v(-76.5, 29.84) * mm, v(-78.4, 28.97) * mm, v(-79.9, 28.55) * mm], "startDerivative": vector(-65.6, -51.95) * mm, "endDerivative": vector(-54.28, -13.22) * mm});
            skLineSegment(sketch, "E58", {"start": v(-16.9, 34.22) * mm, "end": v(-16.9, 31.96) * mm});
            skFitSpline(sketch, "E59", {"points": [v(-16.9, 31.96) * mm, v(-18.1, 30.95) * mm, v(-19.82, 29.72) * mm, v(-21.63, 28.55) * mm, v(-23.53, 27.5) * mm, v(-25.25, 26.85) * mm, v(-27.13, 26.53) * mm, v(-29.05, 26.56) * mm, v(-31.45, 27.3) * mm, v(-34.55, 29) * mm, v(-37.5, 31.02) * mm, v(-39.84, 32.99) * mm, v(-42.44, 35.13) * mm, v(-44.25, 36.64) * mm, v(-46.14, 38.1) * mm, v(-47.72, 39.24) * mm, v(-49.32, 40.26) * mm, v(-51.05, 41.03) * mm, v(-52.82, 41.6) * mm, v(-55.16, 41.86) * mm, v(-57.51, 41.47) * mm, v(-60.32, 40.09) * mm, v(-63.06, 38.24) * mm, v(-65.76, 36.15) * mm, v(-67.49, 34.57) * mm, v(-70.66, 31.96) * mm, v(-72.37, 30.39) * mm, v(-74.17, 29.1) * mm, v(-75.98, 27.96) * mm, v(-77.76, 27.03) * mm, v(-79.9, 26.21) * mm], "startDerivative": vector(-42.76, -36.86) * mm, "endDerivative": vector(-68.1, -24.19) * mm});
            skLineSegment(sketch, "E60", {"start": v(-79.9, 28.55) * mm, "end": v(-79.9, 26.21) * mm});
            skFitSpline(sketch, "E61", {"points": [v(-16.9, 30.74) * mm, v(-19.25, 28.9) * mm, v(-21.18, 27.54) * mm, v(-23.18, 26.5) * mm, v(-25, 25.7) * mm, v(-27.08, 25.27) * mm, v(-28.89, 25.35) * mm, v(-31.24, 26) * mm, v(-33.28, 26.96) * mm, v(-35.6, 28.47) * mm, v(-37.98, 30.28) * mm, v(-40.6, 32.4) * mm, v(-43.3, 34.67) * mm, v(-45.92, 36.8) * mm, v(-47.77, 38.1) * mm, v(-49.55, 39.16) * mm, v(-51.69, 40.07) * mm, v(-52.99, 40.42) * mm, v(-54.31, 40.62) * mm, v(-56.45, 40.49) * mm, v(-58.72, 39.78) * mm, v(-61.18, 38.45) * mm, v(-63.97, 36.45) * mm, v(-65.94, 34.75) * mm, v(-68.23, 32.78) * mm, v(-70.75, 30.63) * mm, v(-72.95, 28.8) * mm, v(-74.77, 27.47) * mm, v(-76.5, 26.36) * mm, v(-78.4, 25.49) * mm, v(-79.9, 25.07) * mm], "startDerivative": vector(-65.6, -51.95) * mm, "endDerivative": vector(-54.28, -13.22) * mm});
            skLineSegment(sketch, "E62", {"start": v(-16.9, 30.74) * mm, "end": v(-16.9, 28.48) * mm});
            skFitSpline(sketch, "E63", {"points": [v(-16.9, 28.48) * mm, v(-18.1, 27.48) * mm, v(-19.82, 26.24) * mm, v(-21.63, 25.07) * mm, v(-23.53, 24.02) * mm, v(-25.25, 23.37) * mm, v(-27.13, 23.05) * mm, v(-29.05, 23.08) * mm, v(-31.45, 23.81) * mm, v(-34.55, 25.53) * mm, v(-37.5, 27.54) * mm, v(-39.84, 29.51) * mm, v(-42.44, 31.65) * mm, v(-44.25, 33.16) * mm, v(-46.14, 34.62) * mm, v(-47.72, 35.76) * mm, v(-49.32, 36.78) * mm, v(-51.05, 37.55) * mm, v(-52.82, 38.13) * mm, v(-55.16, 38.38) * mm, v(-57.51, 38) * mm, v(-60.32, 36.6) * mm, v(-63.06, 34.76) * mm, v(-65.76, 32.68) * mm, v(-67.49, 31.1) * mm, v(-70.66, 28.48) * mm, v(-72.37, 26.9) * mm, v(-74.17, 25.63) * mm, v(-75.98, 24.48) * mm, v(-77.76, 23.55) * mm, v(-79.9, 22.73) * mm], "startDerivative": vector(-42.76, -36.86) * mm, "endDerivative": vector(-68.1, -24.19) * mm});
            skLineSegment(sketch, "E64", {"start": v(-79.9, 25.07) * mm, "end": v(-79.9, 22.73) * mm});
            skFitSpline(sketch, "E65", {"points": [v(-16.9, 27.19) * mm, v(-19.25, 25.34) * mm, v(-21.18, 23.99) * mm, v(-23.18, 22.95) * mm, v(-25, 22.14) * mm, v(-27.08, 21.71) * mm, v(-28.89, 21.79) * mm, v(-31.24, 22.44) * mm, v(-33.28, 23.4) * mm, v(-35.6, 24.91) * mm, v(-37.98, 26.72) * mm, v(-40.6, 28.84) * mm, v(-43.3, 31.12) * mm, v(-45.92, 33.24) * mm, v(-47.77, 34.54) * mm, v(-49.55, 35.6) * mm, v(-51.69, 36.51) * mm, v(-52.99, 36.87) * mm, v(-54.31, 37.06) * mm, v(-56.45, 36.93) * mm, v(-58.72, 36.22) * mm, v(-61.18, 34.9) * mm, v(-63.97, 32.9) * mm, v(-65.94, 31.2) * mm, v(-68.23, 29.23) * mm, v(-70.75, 27.07) * mm, v(-72.95, 25.24) * mm, v(-74.77, 23.91) * mm, v(-76.5, 22.8) * mm, v(-78.4, 21.93) * mm, v(-79.9, 21.51) * mm], "startDerivative": vector(-65.6, -51.95) * mm, "endDerivative": vector(-54.28, -13.22) * mm});
            skLineSegment(sketch, "E66", {"start": v(-16.9, 27.19) * mm, "end": v(-16.9, 24.93) * mm});
            skFitSpline(sketch, "E67", {"points": [v(-16.9, 24.93) * mm, v(-18.1, 23.92) * mm, v(-19.82, 22.68) * mm, v(-21.63, 21.51) * mm, v(-23.53, 20.46) * mm, v(-25.25, 19.82) * mm, v(-27.13, 19.5) * mm, v(-29.05, 19.52) * mm, v(-31.45, 20.26) * mm, v(-34.55, 21.98) * mm, v(-37.5, 23.99) * mm, v(-39.84, 25.95) * mm, v(-42.44, 28.1) * mm, v(-44.25, 29.6) * mm, v(-46.14, 31.07) * mm, v(-47.72, 32.2) * mm, v(-49.32, 33.22) * mm, v(-51.05, 34) * mm, v(-52.82, 34.57) * mm, v(-55.16, 34.82) * mm, v(-57.51, 34.44) * mm, v(-60.32, 33.05) * mm, v(-63.06, 31.2) * mm, v(-65.76, 29.12) * mm, v(-67.49, 27.54) * mm, v(-70.66, 24.93) * mm, v(-72.37, 23.35) * mm, v(-74.17, 22.07) * mm, v(-75.98, 20.92) * mm, v(-77.76, 20) * mm, v(-79.9, 19.18) * mm], "startDerivative": vector(-42.76, -36.86) * mm, "endDerivative": vector(-68.1, -24.19) * mm});
            skLineSegment(sketch, "E68", {"start": v(-79.9, 21.51) * mm, "end": v(-79.9, 19.18) * mm});
            skFitSpline(sketch, "E69", {"points": [v(-16.9, 23.56) * mm, v(-19.25, 21.7) * mm, v(-21.18, 20.35) * mm, v(-23.18, 19.31) * mm, v(-25, 18.5) * mm, v(-27.08, 18.08) * mm, v(-28.89, 18.16) * mm, v(-31.24, 18.81) * mm, v(-33.28, 19.78) * mm, v(-35.6, 21.28) * mm, v(-37.98, 23.1) * mm, v(-40.6, 25.2) * mm, v(-43.3, 27.48) * mm, v(-45.92, 29.6) * mm, v(-47.77, 30.9) * mm, v(-49.55, 31.97) * mm, v(-51.69, 32.88) * mm, v(-52.99, 33.24) * mm, v(-54.31, 33.43) * mm, v(-56.45, 33.3) * mm, v(-58.72, 32.59) * mm, v(-61.18, 31.26) * mm, v(-63.97, 29.26) * mm, v(-65.94, 27.57) * mm, v(-68.23, 25.6) * mm, v(-70.75, 23.44) * mm, v(-72.95, 21.6) * mm, v(-74.77, 20.28) * mm, v(-76.5, 19.18) * mm, v(-78.4, 18.3) * mm, v(-79.9, 17.88) * mm], "startDerivative": vector(-65.6, -51.95) * mm, "endDerivative": vector(-54.28, -13.22) * mm});
            skLineSegment(sketch, "E70", {"start": v(-16.9, 23.56) * mm, "end": v(-16.9, 21.3) * mm});
            skFitSpline(sketch, "E71", {"points": [v(-16.9, 21.3) * mm, v(-18.1, 20.29) * mm, v(-19.82, 19.05) * mm, v(-21.63, 17.88) * mm, v(-23.53, 16.83) * mm, v(-25.25, 16.19) * mm, v(-27.13, 15.87) * mm, v(-29.05, 15.9) * mm, v(-31.45, 16.63) * mm, v(-34.55, 18.34) * mm, v(-37.5, 20.35) * mm, v(-39.84, 22.32) * mm, v(-42.44, 24.47) * mm, v(-44.25, 25.97) * mm, v(-46.14, 27.43) * mm, v(-47.72, 28.57) * mm, v(-49.32, 29.6) * mm, v(-51.05, 30.36) * mm, v(-52.82, 30.94) * mm, v(-55.16, 31.2) * mm, v(-57.51, 30.8) * mm, v(-60.32, 29.42) * mm, v(-63.06, 27.57) * mm, v(-65.76, 25.49) * mm, v(-67.49, 23.9) * mm, v(-70.66, 21.3) * mm, v(-72.37, 19.72) * mm, v(-74.17, 18.44) * mm, v(-75.98, 17.29) * mm, v(-77.76, 16.36) * mm, v(-79.9, 15.55) * mm], "startDerivative": vector(-42.76, -36.86) * mm, "endDerivative": vector(-68.1, -24.19) * mm});
            skLineSegment(sketch, "E72", {"start": v(-79.9, 17.88) * mm, "end": v(-79.9, 15.55) * mm});
            skFitSpline(sketch, "E73", {"points": [v(-16.9, 19.8) * mm, v(-19.25, 17.94) * mm, v(-21.18, 16.6) * mm, v(-23.18, 15.55) * mm, v(-25, 14.75) * mm, v(-27.08, 14.32) * mm, v(-28.89, 14.4) * mm, v(-31.24, 15.05) * mm, v(-33.28, 16.02) * mm, v(-35.6, 17.52) * mm, v(-37.98, 19.33) * mm, v(-40.6, 21.45) * mm, v(-43.3, 23.72) * mm, v(-45.92, 25.85) * mm, v(-47.77, 27.14) * mm, v(-49.55, 28.21) * mm, v(-51.69, 29.12) * mm, v(-52.99, 29.48) * mm, v(-54.31, 29.67) * mm, v(-56.45, 29.54) * mm, v(-58.72, 28.83) * mm, v(-61.18, 27.5) * mm, v(-63.97, 25.5) * mm, v(-65.94, 23.8) * mm, v(-68.23, 21.84) * mm, v(-70.75, 19.68) * mm, v(-72.95, 17.85) * mm, v(-74.77, 16.52) * mm, v(-76.5, 15.42) * mm, v(-78.4, 14.54) * mm, v(-79.9, 14.12) * mm], "startDerivative": vector(-65.6, -51.95) * mm, "endDerivative": vector(-54.28, -13.22) * mm});
            skLineSegment(sketch, "E74", {"start": v(-16.9, 19.8) * mm, "end": v(-16.9, 17.54) * mm});
            skFitSpline(sketch, "E75", {"points": [v(-16.9, 17.54) * mm, v(-18.1, 16.53) * mm, v(-19.82, 15.3) * mm, v(-21.63, 14.12) * mm, v(-23.53, 13.07) * mm, v(-25.25, 12.43) * mm, v(-27.13, 12.1) * mm, v(-29.05, 12.13) * mm, v(-31.45, 12.87) * mm, v(-34.55, 14.58) * mm, v(-37.5, 16.6) * mm, v(-39.84, 18.56) * mm, v(-42.44, 20.7) * mm, v(-44.25, 22.2) * mm, v(-46.14, 23.67) * mm, v(-47.72, 24.81) * mm, v(-49.32, 25.83) * mm, v(-51.05, 26.6) * mm, v(-52.82, 27.18) * mm, v(-55.16, 27.43) * mm, v(-57.51, 27.05) * mm, v(-60.32, 25.66) * mm, v(-63.06, 23.8) * mm, v(-65.76, 21.73) * mm, v(-67.49, 20.15) * mm, v(-70.66, 17.54) * mm, v(-72.37, 15.96) * mm, v(-74.17, 14.68) * mm, v(-75.98, 13.53) * mm, v(-77.76, 12.6) * mm, v(-79.9, 11.79) * mm], "startDerivative": vector(-42.76, -36.86) * mm, "endDerivative": vector(-68.1, -24.19) * mm});
            skLineSegment(sketch, "E76", {"start": v(-79.9, 14.12) * mm, "end": v(-79.9, 11.79) * mm});
            skFitSpline(sketch, "E77", {"points": [v(-16.9, 16.11) * mm, v(-19.25, 14.26) * mm, v(-21.18, 12.91) * mm, v(-23.18, 11.87) * mm, v(-25, 11.06) * mm, v(-27.08, 10.64) * mm, v(-28.89, 10.72) * mm, v(-31.24, 11.37) * mm, v(-33.28, 12.33) * mm, v(-35.6, 13.84) * mm, v(-37.98, 15.65) * mm, v(-40.6, 17.77) * mm, v(-43.3, 20.04) * mm, v(-45.92, 22.16) * mm, v(-47.77, 23.46) * mm, v(-49.55, 24.53) * mm, v(-51.69, 25.44) * mm, v(-52.99, 25.8) * mm, v(-54.31, 25.99) * mm, v(-56.45, 25.86) * mm, v(-58.72, 25.15) * mm, v(-61.18, 23.82) * mm, v(-63.97, 21.82) * mm, v(-65.94, 20.12) * mm, v(-68.23, 18.15) * mm, v(-70.75, 16) * mm, v(-72.95, 14.17) * mm, v(-74.77, 12.84) * mm, v(-76.5, 11.73) * mm, v(-78.4, 10.86) * mm, v(-79.9, 10.44) * mm], "startDerivative": vector(-65.6, -51.95) * mm, "endDerivative": vector(-54.28, -13.22) * mm});
            skLineSegment(sketch, "E78", {"start": v(-16.9, 16.11) * mm, "end": v(-16.9, 13.85) * mm});
            skFitSpline(sketch, "E79", {"points": [v(-16.9, 13.85) * mm, v(-18.1, 12.85) * mm, v(-19.82, 11.6) * mm, v(-21.63, 10.44) * mm, v(-23.53, 9.39) * mm, v(-25.25, 8.74) * mm, v(-27.13, 8.42) * mm, v(-29.05, 8.45) * mm, v(-31.45, 9.18) * mm, v(-34.55, 10.9) * mm, v(-37.5, 12.91) * mm, v(-39.84, 14.88) * mm, v(-42.44, 17.02) * mm, v(-44.25, 18.53) * mm, v(-46.14, 20) * mm, v(-47.72, 21.13) * mm, v(-49.32, 22.15) * mm, v(-51.05, 22.92) * mm, v(-52.82, 23.5) * mm, v(-55.16, 23.75) * mm, v(-57.51, 23.36) * mm, v(-60.32, 21.98) * mm, v(-63.06, 20.13) * mm, v(-65.76, 18.05) * mm, v(-67.49, 16.46) * mm, v(-70.66, 13.85) * mm, v(-72.37, 12.28) * mm, v(-74.17, 11) * mm, v(-75.98, 9.85) * mm, v(-77.76, 8.92) * mm, v(-79.9, 8.1) * mm], "startDerivative": vector(-42.76, -36.86) * mm, "endDerivative": vector(-68.1, -24.19) * mm});
            skLineSegment(sketch, "E80", {"start": v(-79.9, 10.44) * mm, "end": v(-79.9, 8.1) * mm});
            skFitSpline(sketch, "E81", {"points": [v(-16.9, 12.33) * mm, v(-19.25, 10.48) * mm, v(-21.18, 9.13) * mm, v(-23.18, 8.09) * mm, v(-25, 7.28) * mm, v(-27.08, 6.85) * mm, v(-28.89, 6.93) * mm, v(-31.24, 7.59) * mm, v(-33.28, 8.55) * mm, v(-35.6, 10.05) * mm, v(-37.98, 11.86) * mm, v(-40.6, 13.98) * mm, v(-43.3, 16.26) * mm, v(-45.92, 18.38) * mm, v(-47.77, 19.68) * mm, v(-49.55, 20.75) * mm, v(-51.69, 21.65) * mm, v(-52.99, 22) * mm, v(-54.31, 22.2) * mm, v(-56.45, 22.07) * mm, v(-58.72, 21.36) * mm, v(-61.18, 20.03) * mm, v(-63.97, 18.04) * mm, v(-65.94, 16.34) * mm, v(-68.23, 14.37) * mm, v(-70.75, 12.21) * mm, v(-72.95, 10.38) * mm, v(-74.77, 9.05) * mm, v(-76.5, 7.95) * mm, v(-78.4, 7.07) * mm, v(-79.9, 6.65) * mm], "startDerivative": vector(-65.6, -51.95) * mm, "endDerivative": vector(-54.28, -13.22) * mm});
            skLineSegment(sketch, "E82", {"start": v(-16.9, 12.33) * mm, "end": v(-16.9, 10.07) * mm});
            skFitSpline(sketch, "E83", {"points": [v(-16.9, 10.07) * mm, v(-18.1, 9.06) * mm, v(-19.82, 7.82) * mm, v(-21.63, 6.65) * mm, v(-23.53, 5.6) * mm, v(-25.25, 4.96) * mm, v(-27.13, 4.64) * mm, v(-29.05, 4.66) * mm, v(-31.45, 5.4) * mm, v(-34.55, 7.12) * mm, v(-37.5, 9.13) * mm, v(-39.84, 11.1) * mm, v(-42.44, 13.24) * mm, v(-44.25, 14.74) * mm, v(-46.14, 16.2) * mm, v(-47.72, 17.34) * mm, v(-49.32, 18.36) * mm, v(-51.05, 19.14) * mm, v(-52.82, 19.71) * mm, v(-55.16, 19.96) * mm, v(-57.51, 19.58) * mm, v(-60.32, 18.2) * mm, v(-63.06, 16.34) * mm, v(-65.76, 14.26) * mm, v(-67.49, 12.68) * mm, v(-70.66, 10.07) * mm, v(-72.37, 8.5) * mm, v(-74.17, 7.21) * mm, v(-75.98, 6.06) * mm, v(-77.76, 5.14) * mm, v(-79.9, 4.32) * mm], "startDerivative": vector(-42.76, -36.86) * mm, "endDerivative": vector(-68.1, -24.19) * mm});
            skLineSegment(sketch, "E84", {"start": v(-79.9, 6.65) * mm, "end": v(-79.9, 4.32) * mm});
            skFitSpline(sketch, "E85", {"points": [v(-16.9, 8.7) * mm, v(-19.25, 6.84) * mm, v(-21.18, 5.5) * mm, v(-23.18, 4.45) * mm, v(-25, 3.65) * mm, v(-27.08, 3.22) * mm, v(-28.89, 3.3) * mm, v(-31.24, 3.95) * mm, v(-33.28, 4.92) * mm, v(-35.6, 6.42) * mm, v(-37.98, 8.23) * mm, v(-40.6, 10.35) * mm, v(-43.3, 12.62) * mm, v(-45.92, 14.75) * mm, v(-47.77, 16.04) * mm, v(-49.55, 17.11) * mm, v(-51.69, 18.02) * mm, v(-52.99, 18.38) * mm, v(-54.31, 18.57) * mm, v(-56.45, 18.44) * mm, v(-58.72, 17.73) * mm, v(-61.18, 16.4) * mm, v(-63.97, 14.4) * mm, v(-65.94, 12.7) * mm, v(-68.23, 10.74) * mm, v(-70.75, 8.58) * mm, v(-72.95, 6.75) * mm, v(-74.77, 5.42) * mm, v(-76.5, 4.32) * mm, v(-78.4, 3.44) * mm, v(-79.9, 3.02) * mm], "startDerivative": vector(-65.6, -51.95) * mm, "endDerivative": vector(-54.28, -13.22) * mm});
            skLineSegment(sketch, "E86", {"start": v(-16.9, 8.7) * mm, "end": v(-16.9, 6.44) * mm});
            skFitSpline(sketch, "E87", {"points": [v(-16.9, 6.44) * mm, v(-18.1, 5.43) * mm, v(-19.82, 4.2) * mm, v(-21.63, 3.02) * mm, v(-23.53, 1.97) * mm, v(-25.25, 1.33) * mm, v(-27.13, 1) * mm, v(-29.05, 1.03) * mm, v(-31.45, 1.77) * mm, v(-34.55, 3.48) * mm, v(-37.5, 5.5) * mm, v(-39.84, 7.46) * mm, v(-42.44, 9.6) * mm, v(-44.25, 11.11) * mm, v(-46.14, 12.57) * mm, v(-47.72, 13.71) * mm, v(-49.32, 14.73) * mm, v(-51.05, 15.5) * mm, v(-52.82, 16.08) * mm, v(-55.16, 16.33) * mm, v(-57.51, 15.95) * mm, v(-60.32, 14.56) * mm, v(-63.06, 12.7) * mm, v(-65.76, 10.63) * mm, v(-67.49, 9.05) * mm, v(-70.66, 6.44) * mm, v(-72.37, 4.86) * mm, v(-74.17, 3.58) * mm, v(-75.98, 2.43) * mm, v(-77.76, 1.5) * mm, v(-79.9, 0.69) * mm], "startDerivative": vector(-42.76, -36.86) * mm, "endDerivative": vector(-68.1, -24.19) * mm});
            skLineSegment(sketch, "E88", {"start": v(-79.9, 3.02) * mm, "end": v(-79.9, 0.69) * mm});
            skFitSpline(sketch, "E89", {"points": [v(-16.9, 5.22) * mm, v(-19.25, 3.36) * mm, v(-21.18, 2.02) * mm, v(-23.18, 0.97) * mm, v(-25, 0.17) * mm, v(-27.08, -0.26) * mm, v(-28.89, -0.18) * mm, v(-31.24, 0.47) * mm, v(-33.28, 1.44) * mm, v(-35.6, 2.94) * mm, v(-37.98, 4.75) * mm, v(-40.6, 6.87) * mm, v(-43.3, 9.14) * mm, v(-45.92, 11.27) * mm, v(-47.77, 12.56) * mm, v(-49.55, 13.63) * mm, v(-51.69, 14.54) * mm, v(-52.99, 14.9) * mm, v(-54.31, 15.1) * mm, v(-56.45, 14.96) * mm, v(-58.72, 14.25) * mm, v(-61.18, 12.92) * mm, v(-63.97, 10.92) * mm, v(-65.94, 9.23) * mm, v(-68.23, 7.26) * mm, v(-70.75, 5.1) * mm, v(-72.95, 3.27) * mm, v(-74.77, 1.94) * mm, v(-76.5, 0.84) * mm, v(-78.4, -0.04) * mm, v(-79.9, -0.46) * mm], "startDerivative": vector(-65.6, -51.95) * mm, "endDerivative": vector(-54.28, -13.22) * mm});
            skLineSegment(sketch, "E90", {"start": v(-16.9, 5.22) * mm, "end": v(-16.9, 2.96) * mm});
            skFitSpline(sketch, "E91", {"points": [v(-16.9, 2.96) * mm, v(-18.1, 1.95) * mm, v(-19.82, 0.71) * mm, v(-21.63, -0.46) * mm, v(-23.53, -1.51) * mm, v(-25.25, -2.15) * mm, v(-27.13, -2.47) * mm, v(-29.05, -2.45) * mm, v(-31.45, -1.71) * mm, v(-34.55, 0) * mm, v(-37.5, 2.02) * mm, v(-39.84, 3.98) * mm, v(-42.44, 6.13) * mm, v(-44.25, 7.63) * mm, v(-46.14, 9.1) * mm, v(-47.72, 10.23) * mm, v(-49.32, 11.25) * mm, v(-51.05, 12.02) * mm, v(-52.82, 12.6) * mm, v(-55.16, 12.85) * mm, v(-57.51, 12.47) * mm, v(-60.32, 11.08) * mm, v(-63.06, 9.23) * mm, v(-65.76, 7.15) * mm, v(-67.49, 5.57) * mm, v(-70.66, 2.96) * mm, v(-72.37, 1.38) * mm, v(-74.17, 0.1) * mm, v(-75.98, -1.05) * mm, v(-77.76, -1.98) * mm, v(-79.9, -2.8) * mm], "startDerivative": vector(-42.76, -36.86) * mm, "endDerivative": vector(-68.1, -24.19) * mm});
            skFitSpline(sketch, "E92", {"points": [v(-16.89, 1.34) * mm, v(-19.25, -0.5) * mm, v(-21.18, -1.85) * mm, v(-23.18, -2.89) * mm, v(-25, -3.7) * mm, v(-27.08, -4.12) * mm, v(-28.89, -4.04) * mm, v(-31.24, -3.39) * mm, v(-33.28, -2.42) * mm, v(-35.6, -0.92) * mm, v(-37.98, 0.9) * mm, v(-40.6, 3) * mm, v(-43.3, 5.28) * mm, v(-45.92, 7.4) * mm, v(-47.77, 8.7) * mm, v(-49.55, 9.77) * mm, v(-51.69, 10.68) * mm, v(-52.99, 11.04) * mm, v(-54.31, 11.23) * mm, v(-56.45, 11.1) * mm, v(-58.72, 10.39) * mm, v(-61.18, 9.06) * mm, v(-63.97, 7.06) * mm, v(-65.94, 5.37) * mm, v(-68.23, 3.4) * mm, v(-70.75, 1.24) * mm, v(-72.95, -0.6) * mm, v(-74.77, -1.92) * mm, v(-76.5, -3.02) * mm, v(-78.4, -3.9) * mm, v(-79.9, -4.32) * mm], "startDerivative": vector(-65.6, -51.95) * mm, "endDerivative": vector(-54.28, -13.22) * mm});
            skLineSegment(sketch, "E93", {"start": v(-16.89, 1.34) * mm, "end": v(-16.89, -0.36) * mm});
            skFitSpline(sketch, "E94", {"points": [v(-16.89, -0.92) * mm, v(-18.1, -1.91) * mm, v(-19.82, -3.15) * mm, v(-21.63, -4.32) * mm, v(-23.53, -5.37) * mm, v(-25.25, -6.01) * mm, v(-27.13, -6.33) * mm, v(-29.05, -6.3) * mm, v(-31.45, -5.57) * mm, v(-34.55, -3.86) * mm, v(-37.5, -1.85) * mm, v(-39.84, 0.12) * mm, v(-42.44, 2.27) * mm, v(-44.25, 3.77) * mm, v(-46.14, 5.23) * mm, v(-47.72, 6.37) * mm, v(-49.32, 7.4) * mm, v(-51.05, 8.16) * mm, v(-52.82, 8.74) * mm, v(-55.16, 9) * mm, v(-57.51, 8.6) * mm, v(-60.32, 7.22) * mm, v(-63.06, 5.37) * mm, v(-65.76, 3.29) * mm, v(-67.49, 1.7) * mm, v(-70.66, -0.92) * mm, v(-72.37, -2.48) * mm, v(-74.17, -3.76) * mm, v(-75.98, -4.91) * mm, v(-77.76, -5.84) * mm, v(-79.9, -6.65) * mm], "startDerivative": vector(-42.76, -36.86) * mm, "endDerivative": vector(-68.1, -24.19) * mm});
            skLineSegment(sketch, "E95", {"start": v(-79.9, -4.32) * mm, "end": v(-79.9, -6.65) * mm});
            skFitSpline(sketch, "E96", {"points": [v(-16.9, -1.97) * mm, v(-19.25, -3.82) * mm, v(-21.18, -5.17) * mm, v(-23.18, -6.21) * mm, v(-25, -7.02) * mm, v(-27.08, -7.45) * mm, v(-28.89, -7.37) * mm, v(-31.24, -6.71) * mm, v(-33.28, -5.75) * mm, v(-35.6, -4.25) * mm, v(-37.98, -2.44) * mm, v(-40.6, -0.32) * mm, v(-43.3, 1.96) * mm, v(-45.92, 4.08) * mm, v(-47.77, 5.38) * mm, v(-49.55, 6.45) * mm, v(-51.69, 7.35) * mm, v(-52.99, 7.7) * mm, v(-54.31, 7.9) * mm, v(-56.45, 7.77) * mm, v(-58.72, 7.06) * mm, v(-61.18, 5.73) * mm, v(-63.97, 3.73) * mm, v(-65.94, 2.04) * mm, v(-68.23, 0.07) * mm, v(-70.75, -2.09) * mm, v(-72.95, -3.92) * mm, v(-74.77, -5.25) * mm, v(-76.5, -6.35) * mm, v(-78.4, -7.23) * mm, v(-79.9, -7.65) * mm], "startDerivative": vector(-65.6, -51.95) * mm, "endDerivative": vector(-54.28, -13.22) * mm});
            skLineSegment(sketch, "E97", {"start": v(-16.9, -1.97) * mm, "end": v(-16.9, -4.23) * mm});
            skFitSpline(sketch, "E98", {"points": [v(-16.9, -4.23) * mm, v(-18.1, -5.24) * mm, v(-19.82, -6.48) * mm, v(-21.63, -7.65) * mm, v(-23.53, -8.7) * mm, v(-25.25, -9.34) * mm, v(-27.13, -9.66) * mm, v(-29.05, -9.64) * mm, v(-31.45, -8.9) * mm, v(-34.55, -7.18) * mm, v(-37.5, -5.17) * mm, v(-39.84, -3.2) * mm, v(-42.44, -1.06) * mm, v(-44.25, 0.44) * mm, v(-46.14, 1.9) * mm, v(-47.72, 3.04) * mm, v(-49.32, 4.06) * mm, v(-51.05, 4.84) * mm, v(-52.82, 5.41) * mm, v(-55.16, 5.66) * mm, v(-57.51, 5.28) * mm, v(-60.32, 3.9) * mm, v(-63.06, 2.04) * mm, v(-65.76, -0.04) * mm, v(-67.49, -1.62) * mm, v(-70.66, -4.23) * mm, v(-72.37, -5.8) * mm, v(-74.17, -7.09) * mm, v(-75.98, -8.24) * mm, v(-77.76, -9.16) * mm, v(-79.9, -9.98) * mm], "startDerivative": vector(-42.76, -36.86) * mm, "endDerivative": vector(-68.1, -24.19) * mm});
            skLineSegment(sketch, "E99", {"start": v(-79.9, -7.65) * mm, "end": v(-79.9, -9.98) * mm});
            skFitSpline(sketch, "E100", {"points": [v(-16.9, -5.78) * mm, v(-19.25, -7.63) * mm, v(-21.18, -8.98) * mm, v(-23.18, -10.02) * mm, v(-25, -10.83) * mm, v(-27.08, -11.26) * mm, v(-28.89, -11.18) * mm, v(-31.24, -10.52) * mm, v(-33.28, -9.56) * mm, v(-35.6, -8.06) * mm, v(-37.98, -6.25) * mm, v(-40.6, -4.13) * mm, v(-43.3, -1.85) * mm, v(-45.92, 0.27) * mm, v(-47.77, 1.57) * mm, v(-49.55, 2.64) * mm, v(-51.69, 3.54) * mm, v(-52.99, 3.9) * mm, v(-54.31, 4.1) * mm, v(-56.45, 3.96) * mm, v(-58.72, 3.25) * mm, v(-61.18, 1.92) * mm, v(-63.97, -0.08) * mm, v(-65.94, -1.77) * mm, v(-68.23, -3.74) * mm, v(-70.75, -5.9) * mm, v(-72.95, -7.73) * mm, v(-74.77, -9.06) * mm, v(-76.5, -10.16) * mm, v(-78.4, -11.04) * mm, v(-79.9, -11.46) * mm], "startDerivative": vector(-65.6, -51.95) * mm, "endDerivative": vector(-54.28, -13.22) * mm});
            skLineSegment(sketch, "E101", {"start": v(-16.9, -5.78) * mm, "end": v(-16.9, -8.04) * mm});
            skFitSpline(sketch, "E102", {"points": [v(-16.9, -8.04) * mm, v(-18.1, -9.05) * mm, v(-19.82, -10.29) * mm, v(-21.63, -11.46) * mm, v(-23.53, -12.5) * mm, v(-25.25, -13.15) * mm, v(-27.13, -13.47) * mm, v(-29.05, -13.45) * mm, v(-31.45, -12.71) * mm, v(-34.55, -11) * mm, v(-37.5, -8.98) * mm, v(-39.84, -7.02) * mm, v(-42.44, -4.87) * mm, v(-44.25, -3.37) * mm, v(-46.14, -1.9) * mm, v(-47.72, -0.77) * mm, v(-49.32, 0.25) * mm, v(-51.05, 1.03) * mm, v(-52.82, 1.6) * mm, v(-55.16, 1.85) * mm, v(-57.51, 1.47) * mm, v(-60.32, 0.08) * mm, v(-63.06, -1.77) * mm, v(-65.76, -3.85) * mm, v(-67.49, -5.43) * mm, v(-70.66, -8.04) * mm, v(-72.37, -9.62) * mm, v(-74.17, -10.9) * mm, v(-75.98, -12.05) * mm, v(-77.76, -12.97) * mm, v(-79.9, -13.8) * mm], "startDerivative": vector(-42.76, -36.86) * mm, "endDerivative": vector(-68.1, -24.19) * mm});
            skLineSegment(sketch, "E103", {"start": v(-79.9, -11.46) * mm, "end": v(-79.9, -13.8) * mm});
            skFitSpline(sketch, "E104", {"points": [v(-16.89, -9.18) * mm, v(-19.25, -11.01) * mm, v(-21.18, -12.36) * mm, v(-23.18, -13.4) * mm, v(-25, -14.21) * mm, v(-27.08, -14.64) * mm, v(-28.89, -14.56) * mm, v(-31.24, -13.9) * mm, v(-33.28, -12.94) * mm, v(-35.6, -11.44) * mm, v(-37.98, -9.63) * mm, v(-40.6, -7.5) * mm, v(-43.3, -5.23) * mm, v(-45.92, -3.1) * mm, v(-47.77, -1.81) * mm, v(-49.55, -0.74) * mm, v(-51.69, 0.16) * mm, v(-52.99, 0.52) * mm, v(-54.31, 0.72) * mm, v(-56.45, 0.59) * mm, v(-58.72, -0.13) * mm, v(-61.18, -1.46) * mm, v(-63.97, -3.45) * mm, v(-65.94, -5.15) * mm, v(-68.23, -7.12) * mm, v(-70.75, -9.27) * mm, v(-72.95, -11.1) * mm, v(-74.77, -12.44) * mm, v(-76.5, -13.54) * mm, v(-78.4, -14.41) * mm, v(-79.9, -14.84) * mm], "startDerivative": vector(-65.6, -51.95) * mm, "endDerivative": vector(-54.28, -13.22) * mm});
            skLineSegment(sketch, "E105", {"start": v(-16.89, -9.18) * mm, "end": v(-16.89, -11.44) * mm});
            skLineSegment(sketch, "E106", {"start": v(-79.9, -14.84) * mm, "end": v(-79.9, -17.17) * mm});
            skLineSegment(sketch, "E107", {"start": v(-79.9, 81.92) * mm, "end": v(-16.9, 81.71) * mm});
            skPoint(sketch, "E108.10.internal.orphan", {"position": v(-37.5, -12.36) * mm});
            skPoint(sketch, "E108.25.internal.orphan", {"position": v(-70.66, -11.44) * mm});
            skPoint(sketch, "E108.30.internal.orphan", {"position": v(-79.9, -17.17) * mm});
            skFitSpline(sketch, "E109.trimOffspring", {"points": [v(-16.89, 1.34) * mm, v(-19.25, -0.5) * mm, v(-21.18, -1.85) * mm, v(-23.18, -2.89) * mm, v(-25, -3.7) * mm, v(-27.08, -4.12) * mm, v(-28.89, -4.04) * mm, v(-31.24, -3.39) * mm, v(-33.28, -2.42) * mm, v(-35.6, -0.92) * mm, v(-37.98, 0.9) * mm, v(-40.6, 3) * mm, v(-43.3, 5.28) * mm, v(-45.92, 7.4) * mm, v(-47.77, 8.7) * mm, v(-49.55, 9.77) * mm, v(-51.69, 10.68) * mm, v(-52.99, 11.04) * mm, v(-54.31, 11.23) * mm, v(-56.45, 11.1) * mm, v(-58.72, 10.39) * mm, v(-61.18, 9.06) * mm, v(-63.97, 7.06) * mm, v(-65.94, 5.37) * mm, v(-68.23, 3.4) * mm, v(-70.75, 1.24) * mm, v(-72.95, -0.6) * mm, v(-74.77, -1.92) * mm, v(-76.5, -3.02) * mm, v(-78.4, -3.9) * mm, v(-79.9, -4.32) * mm], "startDerivative": vector(-65.6, -51.95) * mm, "endDerivative": vector(-54.28, -13.22) * mm});
            skLineSegment(sketch, "E110", {"start": v(-16.89, -0.36) * mm, "end": v(-79.5, -0.36) * mm});
            skSolve(sketch);
        }
        {
            var Q0;
            Q0=qCreatedBy(makeId("Top.planeOp"),FACE);
            var sketch = newSketch(context, id + "F3", { "sketchPlane" : qUnion([Q0])});
            skFitSpline(sketch, "E111", {"points": [v(82.23, 65.45) * mm, v(79.87, 63.6) * mm, v(77.94, 62.25) * mm, v(75.93, 61.21) * mm, v(74.12, 60.4) * mm, v(72.04, 59.98) * mm, v(70.23, 60.05) * mm, v(67.88, 60.7) * mm, v(65.84, 61.67) * mm, v(63.53, 63.18) * mm, v(61.14, 64.99) * mm, v(58.52, 67.1) * mm, v(55.82, 69.38) * mm, v(53.2, 71.5) * mm, v(51.35, 72.8) * mm, v(49.57, 73.87) * mm, v(47.43, 74.78) * mm, v(46.13, 75.13) * mm, v(44.8, 75.33) * mm, v(42.67, 75.2) * mm, v(40.4, 74.49) * mm, v(37.94, 73.16) * mm, v(35.15, 71.16) * mm, v(33.18, 69.46) * mm, v(30.9, 67.5) * mm, v(28.37, 65.34) * mm, v(26.17, 63.5) * mm, v(24.35, 62.18) * mm, v(22.63, 61.07) * mm, v(20.72, 60.2) * mm, v(19.23, 59.78) * mm], "startDerivative": vector(-65.6, -51.95) * mm, "endDerivative": vector(-54.28, -13.22) * mm});
            skFitSpline(sketch, "E112", {"points": [v(82.23, 63.2) * mm, v(81.02, 62.18) * mm, v(79.3, 60.95) * mm, v(77.49, 59.78) * mm, v(75.59, 58.72) * mm, v(73.87, 58.08) * mm, v(71.99, 57.76) * mm, v(70.07, 57.79) * mm, v(67.67, 58.52) * mm, v(64.57, 60.24) * mm, v(61.62, 62.25) * mm, v(59.28, 64.22) * mm, v(56.68, 66.36) * mm, v(54.87, 67.87) * mm, v(52.98, 69.33) * mm, v(51.4, 70.47) * mm, v(49.8, 71.49) * mm, v(48.07, 72.26) * mm, v(46.3, 72.84) * mm, v(43.96, 73.09) * mm, v(41.6, 72.7) * mm, v(38.8, 71.32) * mm, v(36.06, 69.47) * mm, v(33.36, 67.39) * mm, v(31.63, 65.8) * mm, v(28.46, 63.2) * mm, v(26.75, 61.62) * mm, v(24.95, 60.34) * mm, v(23.14, 59.19) * mm, v(21.36, 58.26) * mm, v(19.23, 57.44) * mm], "startDerivative": vector(-42.76, -36.86) * mm, "endDerivative": vector(-68.1, -24.19) * mm});
            skFitSpline(sketch, "E113", {"points": [v(82.23, 69.3) * mm, v(79.87, 67.45) * mm, v(77.94, 66.1) * mm, v(75.93, 65.06) * mm, v(74.12, 64.25) * mm, v(72.04, 63.83) * mm, v(70.23, 63.9) * mm, v(67.88, 64.56) * mm, v(65.84, 65.52) * mm, v(63.53, 67.02) * mm, v(61.14, 68.84) * mm, v(58.52, 70.96) * mm, v(55.82, 73.23) * mm, v(53.2, 75.35) * mm, v(51.35, 76.65) * mm, v(49.57, 77.72) * mm, v(47.43, 78.63) * mm, v(46.13, 78.98) * mm, v(44.8, 79.18) * mm, v(42.67, 79.05) * mm, v(40.4, 78.33) * mm, v(37.94, 77) * mm, v(35.15, 75) * mm, v(33.18, 73.31) * mm, v(30.9, 71.34) * mm, v(28.37, 69.19) * mm, v(26.17, 67.35) * mm, v(24.35, 66.02) * mm, v(22.63, 64.92) * mm, v(20.72, 64.05) * mm, v(19.23, 63.63) * mm], "startDerivative": vector(-65.6, -51.95) * mm, "endDerivative": vector(-54.28, -13.22) * mm});
            skFitSpline(sketch, "E114", {"points": [v(82.23, 67.04) * mm, v(81.02, 66.03) * mm, v(79.3, 64.8) * mm, v(77.49, 63.63) * mm, v(75.59, 62.57) * mm, v(73.87, 61.93) * mm, v(71.99, 61.61) * mm, v(70.07, 61.64) * mm, v(67.67, 62.37) * mm, v(64.57, 64.09) * mm, v(61.62, 66.1) * mm, v(59.28, 68.07) * mm, v(56.68, 70.21) * mm, v(54.87, 71.72) * mm, v(52.98, 73.18) * mm, v(51.4, 74.32) * mm, v(49.8, 75.34) * mm, v(48.07, 76.1) * mm, v(46.3, 76.69) * mm, v(43.96, 76.94) * mm, v(41.6, 76.55) * mm, v(38.8, 75.16) * mm, v(36.06, 73.31) * mm, v(33.36, 71.23) * mm, v(31.63, 69.65) * mm, v(28.46, 67.04) * mm, v(26.75, 65.47) * mm, v(24.95, 64.18) * mm, v(23.14, 63.03) * mm, v(21.36, 62.1) * mm, v(19.23, 61.3) * mm], "startDerivative": vector(-42.76, -36.86) * mm, "endDerivative": vector(-68.1, -24.19) * mm});
            skFitSpline(sketch, "E115", {"points": [v(82.23, 72.86) * mm, v(79.87, 71) * mm, v(77.94, 69.65) * mm, v(75.93, 68.61) * mm, v(74.12, 67.8) * mm, v(72.04, 67.38) * mm, v(70.23, 67.46) * mm, v(67.88, 68.11) * mm, v(65.84, 69.08) * mm, v(63.53, 70.58) * mm, v(61.14, 72.4) * mm, v(58.52, 74.51) * mm, v(55.82, 76.78) * mm, v(53.2, 78.9) * mm, v(51.35, 80.2) * mm, v(49.57, 81.27) * mm, v(47.43, 82.18) * mm, v(46.13, 82.54) * mm, v(44.8, 82.73) * mm, v(42.67, 82.6) * mm, v(40.4, 81.89) * mm, v(37.94, 80.56) * mm, v(35.15, 78.56) * mm, v(33.18, 76.87) * mm, v(30.9, 74.9) * mm, v(28.37, 72.74) * mm, v(26.17, 70.9) * mm, v(24.35, 69.58) * mm, v(22.63, 68.48) * mm, v(20.72, 67.6) * mm, v(19.23, 67.18) * mm], "startDerivative": vector(-65.6, -51.95) * mm, "endDerivative": vector(-54.28, -13.22) * mm});
            skFitSpline(sketch, "E116", {"points": [v(82.23, 70.6) * mm, v(81.02, 69.59) * mm, v(79.3, 68.35) * mm, v(77.49, 67.18) * mm, v(75.59, 66.13) * mm, v(73.87, 65.49) * mm, v(71.99, 65.17) * mm, v(70.07, 65.2) * mm, v(67.67, 65.93) * mm, v(64.57, 67.64) * mm, v(61.62, 69.65) * mm, v(59.28, 71.62) * mm, v(56.68, 73.77) * mm, v(54.87, 75.27) * mm, v(52.98, 76.73) * mm, v(51.4, 77.87) * mm, v(49.8, 78.9) * mm, v(48.07, 79.66) * mm, v(46.3, 80.24) * mm, v(43.96, 80.5) * mm, v(41.6, 80.1) * mm, v(38.8, 78.72) * mm, v(36.06, 76.87) * mm, v(33.36, 74.79) * mm, v(31.63, 73.2) * mm, v(28.46, 70.6) * mm, v(26.75, 69.02) * mm, v(24.95, 67.74) * mm, v(23.14, 66.59) * mm, v(21.36, 65.66) * mm, v(19.23, 64.85) * mm], "startDerivative": vector(-42.76, -36.86) * mm, "endDerivative": vector(-68.1, -24.19) * mm});
            skFitSpline(sketch, "E117", {"points": [v(82.23, 76.51) * mm, v(79.87, 74.66) * mm, v(77.94, 73.31) * mm, v(75.93, 72.27) * mm, v(74.12, 71.46) * mm, v(72.04, 71.04) * mm, v(70.23, 71.11) * mm, v(67.88, 71.77) * mm, v(65.84, 72.73) * mm, v(63.53, 74.24) * mm, v(61.14, 76.05) * mm, v(58.52, 78.17) * mm, v(55.82, 80.44) * mm, v(53.2, 82.56) * mm, v(51.35, 83.86) * mm, v(49.57, 84.93) * mm, v(47.43, 85.84) * mm, v(46.13, 86.2) * mm, v(44.8, 86.39) * mm, v(42.67, 86.26) * mm, v(40.4, 85.54) * mm, v(37.94, 84.22) * mm, v(35.15, 82.22) * mm, v(33.18, 80.52) * mm, v(30.9, 78.55) * mm, v(28.37, 76.4) * mm, v(26.17, 74.56) * mm, v(24.35, 73.23) * mm, v(22.63, 72.13) * mm, v(20.72, 71.26) * mm, v(19.23, 70.84) * mm], "startDerivative": vector(-65.6, -51.95) * mm, "endDerivative": vector(-54.28, -13.22) * mm});
            skFitSpline(sketch, "E118", {"points": [v(82.23, 74.25) * mm, v(81.02, 73.24) * mm, v(79.3, 72) * mm, v(77.49, 70.84) * mm, v(75.59, 69.78) * mm, v(73.87, 69.14) * mm, v(71.99, 68.82) * mm, v(70.07, 68.85) * mm, v(67.67, 69.58) * mm, v(64.57, 71.3) * mm, v(61.62, 73.31) * mm, v(59.28, 75.28) * mm, v(56.68, 77.42) * mm, v(54.87, 78.93) * mm, v(52.98, 80.4) * mm, v(51.4, 81.53) * mm, v(49.8, 82.55) * mm, v(48.07, 83.32) * mm, v(46.3, 83.9) * mm, v(43.96, 84.15) * mm, v(41.6, 83.76) * mm, v(38.8, 82.38) * mm, v(36.06, 80.53) * mm, v(33.36, 78.44) * mm, v(31.63, 76.86) * mm, v(28.46, 74.25) * mm, v(26.75, 72.68) * mm, v(24.95, 71.4) * mm, v(23.14, 70.25) * mm, v(21.36, 69.32) * mm, v(19.23, 68.5) * mm], "startDerivative": vector(-42.76, -36.86) * mm, "endDerivative": vector(-68.1, -24.19) * mm});
            skFitSpline(sketch, "E119", {"points": [v(82.23, 80.34) * mm, v(79.87, 78.48) * mm, v(77.94, 77.13) * mm, v(75.93, 76.1) * mm, v(74.12, 75.28) * mm, v(72.04, 74.86) * mm, v(70.23, 74.94) * mm, v(67.88, 75.6) * mm, v(65.84, 76.56) * mm, v(63.53, 78.06) * mm, v(61.14, 79.87) * mm, v(58.52, 81.99) * mm, v(55.82, 84.26) * mm, v(53.2, 86.39) * mm, v(51.35, 87.68) * mm, v(49.57, 88.75) * mm, v(47.43, 89.66) * mm, v(46.13, 90.02) * mm, v(44.8, 90.21) * mm, v(42.67, 90.08) * mm, v(40.4, 89.37) * mm, v(37.94, 88.04) * mm, v(35.15, 86.04) * mm, v(33.18, 84.35) * mm, v(30.9, 82.38) * mm, v(28.37, 80.22) * mm, v(26.17, 78.39) * mm, v(24.35, 77.06) * mm, v(22.63, 75.96) * mm, v(20.72, 75.08) * mm, v(19.23, 74.66) * mm], "startDerivative": vector(-65.6, -51.95) * mm, "endDerivative": vector(-54.28, -13.22) * mm});
            skFitSpline(sketch, "E120", {"points": [v(82.23, 78.08) * mm, v(81.02, 77.07) * mm, v(79.3, 75.83) * mm, v(77.49, 74.66) * mm, v(75.59, 73.6) * mm, v(73.87, 72.97) * mm, v(71.99, 72.65) * mm, v(70.07, 72.67) * mm, v(67.67, 73.4) * mm, v(64.57, 75.12) * mm, v(61.62, 77.13) * mm, v(59.28, 79.1) * mm, v(56.68, 81.25) * mm, v(54.87, 82.75) * mm, v(52.98, 84.21) * mm, v(51.4, 85.35) * mm, v(49.8, 86.37) * mm, v(48.07, 87.14) * mm, v(46.3, 87.72) * mm, v(43.96, 87.97) * mm, v(41.6, 87.59) * mm, v(38.8, 86.2) * mm, v(36.06, 84.35) * mm, v(33.36, 82.27) * mm, v(31.63, 80.69) * mm, v(28.46, 78.08) * mm, v(26.75, 76.5) * mm, v(24.95, 75.22) * mm, v(23.14, 74.07) * mm, v(21.36, 73.14) * mm, v(19.23, 72.32) * mm], "startDerivative": vector(-42.76, -36.86) * mm, "endDerivative": vector(-68.1, -24.19) * mm});
            skFitSpline(sketch, "E121", {"points": [v(82.23, 61.78) * mm, v(79.87, 59.93) * mm, v(77.94, 58.58) * mm, v(75.93, 57.54) * mm, v(74.12, 56.73) * mm, v(72.04, 56.3) * mm, v(70.23, 56.38) * mm, v(67.88, 57.04) * mm, v(65.84, 58) * mm, v(63.53, 59.5) * mm, v(61.14, 61.32) * mm, v(58.52, 63.44) * mm, v(55.82, 65.7) * mm, v(53.2, 67.83) * mm, v(51.35, 69.13) * mm, v(49.57, 70.2) * mm, v(47.43, 71.1) * mm, v(46.13, 71.46) * mm, v(44.8, 71.66) * mm, v(42.67, 71.53) * mm, v(40.4, 70.81) * mm, v(37.94, 69.49) * mm, v(35.15, 67.49) * mm, v(33.18, 65.8) * mm, v(30.9, 63.82) * mm, v(28.37, 61.67) * mm, v(26.17, 59.83) * mm, v(24.35, 58.5) * mm, v(22.63, 57.4) * mm, v(20.72, 56.53) * mm, v(19.23, 56.1) * mm], "startDerivative": vector(-65.6, -51.95) * mm, "endDerivative": vector(-54.28, -13.22) * mm});
            skFitSpline(sketch, "E122", {"points": [v(82.23, 59.52) * mm, v(81.02, 58.51) * mm, v(79.3, 57.28) * mm, v(77.49, 56.1) * mm, v(75.59, 55.05) * mm, v(73.87, 54.41) * mm, v(71.99, 54.1) * mm, v(70.07, 54.12) * mm, v(67.67, 54.85) * mm, v(64.57, 56.57) * mm, v(61.62, 58.58) * mm, v(59.28, 60.55) * mm, v(56.68, 62.7) * mm, v(54.87, 64.2) * mm, v(52.98, 65.66) * mm, v(51.4, 66.8) * mm, v(49.8, 67.82) * mm, v(48.07, 68.59) * mm, v(46.3, 69.17) * mm, v(43.96, 69.42) * mm, v(41.6, 69.03) * mm, v(38.8, 67.64) * mm, v(36.06, 65.8) * mm, v(33.36, 63.71) * mm, v(31.63, 62.13) * mm, v(28.46, 59.52) * mm, v(26.75, 57.95) * mm, v(24.95, 56.66) * mm, v(23.14, 55.52) * mm, v(21.36, 54.59) * mm, v(19.23, 53.77) * mm], "startDerivative": vector(-42.76, -36.86) * mm, "endDerivative": vector(-68.1, -24.19) * mm});
            skFitSpline(sketch, "E123", {"points": [v(82.23, 58.05) * mm, v(79.87, 56.2) * mm, v(77.94, 54.85) * mm, v(75.93, 53.8) * mm, v(74.12, 53) * mm, v(72.04, 52.57) * mm, v(70.23, 52.65) * mm, v(67.88, 53.3) * mm, v(65.84, 54.27) * mm, v(63.53, 55.77) * mm, v(61.14, 57.58) * mm, v(58.52, 59.7) * mm, v(55.82, 61.98) * mm, v(53.2, 64.1) * mm, v(51.35, 65.4) * mm, v(49.57, 66.46) * mm, v(47.43, 67.37) * mm, v(46.13, 67.73) * mm, v(44.8, 67.92) * mm, v(42.67, 67.8) * mm, v(40.4, 67.08) * mm, v(37.94, 65.75) * mm, v(35.15, 63.75) * mm, v(33.18, 62.06) * mm, v(30.9, 60.09) * mm, v(28.37, 57.93) * mm, v(26.17, 56.1) * mm, v(24.35, 54.77) * mm, v(22.63, 53.67) * mm, v(20.72, 52.8) * mm, v(19.23, 52.37) * mm], "startDerivative": vector(-65.6, -51.95) * mm, "endDerivative": vector(-54.28, -13.22) * mm});
            skFitSpline(sketch, "E124", {"points": [v(82.23, 55.79) * mm, v(81.02, 54.78) * mm, v(79.3, 53.54) * mm, v(77.49, 52.37) * mm, v(75.59, 51.32) * mm, v(73.87, 50.68) * mm, v(71.99, 50.36) * mm, v(70.07, 50.38) * mm, v(67.67, 51.12) * mm, v(64.57, 52.84) * mm, v(61.62, 54.85) * mm, v(59.28, 56.81) * mm, v(56.68, 58.96) * mm, v(54.87, 60.46) * mm, v(52.98, 61.93) * mm, v(51.4, 63.06) * mm, v(49.8, 64.08) * mm, v(48.07, 64.85) * mm, v(46.3, 65.43) * mm, v(43.96, 65.68) * mm, v(41.6, 65.3) * mm, v(38.8, 63.91) * mm, v(36.06, 62.06) * mm, v(33.36, 59.98) * mm, v(31.63, 58.4) * mm, v(28.46, 55.79) * mm, v(26.75, 54.21) * mm, v(24.95, 52.93) * mm, v(23.14, 51.78) * mm, v(21.36, 50.85) * mm, v(19.23, 50.04) * mm], "startDerivative": vector(-42.76, -36.86) * mm, "endDerivative": vector(-68.1, -24.19) * mm});
            skFitSpline(sketch, "E125", {"points": [v(82.23, 54.62) * mm, v(79.87, 52.76) * mm, v(77.94, 51.41) * mm, v(75.93, 50.37) * mm, v(74.12, 49.56) * mm, v(72.04, 49.14) * mm, v(70.23, 49.22) * mm, v(67.88, 49.87) * mm, v(65.84, 50.84) * mm, v(63.53, 52.34) * mm, v(61.14, 54.15) * mm, v(58.52, 56.27) * mm, v(55.82, 58.54) * mm, v(53.2, 60.67) * mm, v(51.35, 61.96) * mm, v(49.57, 63.03) * mm, v(47.43, 63.94) * mm, v(46.13, 64.3) * mm, v(44.8, 64.5) * mm, v(42.67, 64.36) * mm, v(40.4, 63.65) * mm, v(37.94, 62.32) * mm, v(35.15, 60.32) * mm, v(33.18, 58.63) * mm, v(30.9, 56.65) * mm, v(28.37, 54.5) * mm, v(26.17, 52.67) * mm, v(24.35, 51.34) * mm, v(22.63, 50.24) * mm, v(20.72, 49.36) * mm, v(19.23, 48.94) * mm], "startDerivative": vector(-65.6, -51.95) * mm, "endDerivative": vector(-54.28, -13.22) * mm});
            skFitSpline(sketch, "E126", {"points": [v(82.23, 52.36) * mm, v(81.02, 51.35) * mm, v(79.3, 50.1) * mm, v(77.49, 48.94) * mm, v(75.59, 47.89) * mm, v(73.87, 47.25) * mm, v(71.99, 46.92) * mm, v(70.07, 46.95) * mm, v(67.67, 47.69) * mm, v(64.57, 49.4) * mm, v(61.62, 51.41) * mm, v(59.28, 53.38) * mm, v(56.68, 55.53) * mm, v(54.87, 57.03) * mm, v(52.98, 58.5) * mm, v(51.4, 59.63) * mm, v(49.8, 60.65) * mm, v(48.07, 61.42) * mm, v(46.3, 62) * mm, v(43.96, 62.25) * mm, v(41.6, 61.87) * mm, v(38.8, 60.48) * mm, v(36.06, 58.63) * mm, v(33.36, 56.55) * mm, v(31.63, 54.96) * mm, v(28.46, 52.36) * mm, v(26.75, 50.78) * mm, v(24.95, 49.5) * mm, v(23.14, 48.35) * mm, v(21.36, 47.42) * mm, v(19.23, 46.6) * mm], "startDerivative": vector(-42.76, -36.86) * mm, "endDerivative": vector(-68.1, -24.19) * mm});
            skFitSpline(sketch, "E127", {"points": [v(82.23, 50.98) * mm, v(79.87, 49.13) * mm, v(77.94, 47.78) * mm, v(75.93, 46.74) * mm, v(74.12, 45.93) * mm, v(72.04, 45.5) * mm, v(70.23, 45.58) * mm, v(67.88, 46.24) * mm, v(65.84, 47.2) * mm, v(63.53, 48.7) * mm, v(61.14, 50.52) * mm, v(58.52, 52.64) * mm, v(55.82, 54.91) * mm, v(53.2, 57.03) * mm, v(51.35, 58.33) * mm, v(49.57, 59.4) * mm, v(47.43, 60.3) * mm, v(46.13, 60.66) * mm, v(44.8, 60.86) * mm, v(42.67, 60.73) * mm, v(40.4, 60.02) * mm, v(37.94, 58.69) * mm, v(35.15, 56.69) * mm, v(33.18, 55) * mm, v(30.9, 53.02) * mm, v(28.37, 50.87) * mm, v(26.17, 49.04) * mm, v(24.35, 47.7) * mm, v(22.63, 46.6) * mm, v(20.72, 45.73) * mm, v(19.23, 45.3) * mm], "startDerivative": vector(-65.6, -51.95) * mm, "endDerivative": vector(-54.28, -13.22) * mm});
            skFitSpline(sketch, "E128", {"points": [v(82.23, 48.72) * mm, v(81.02, 47.71) * mm, v(79.3, 46.48) * mm, v(77.49, 45.3) * mm, v(75.59, 44.25) * mm, v(73.87, 43.61) * mm, v(71.99, 43.3) * mm, v(70.07, 43.32) * mm, v(67.67, 44.05) * mm, v(64.57, 45.77) * mm, v(61.62, 47.78) * mm, v(59.28, 49.75) * mm, v(56.68, 51.9) * mm, v(54.87, 53.4) * mm, v(52.98, 54.86) * mm, v(51.4, 56) * mm, v(49.8, 57.02) * mm, v(48.07, 57.79) * mm, v(46.3, 58.37) * mm, v(43.96, 58.62) * mm, v(41.6, 58.23) * mm, v(38.8, 56.85) * mm, v(36.06, 55) * mm, v(33.36, 52.92) * mm, v(31.63, 51.33) * mm, v(28.46, 48.72) * mm, v(26.75, 47.15) * mm, v(24.95, 45.87) * mm, v(23.14, 44.72) * mm, v(21.36, 43.79) * mm, v(19.23, 42.97) * mm], "startDerivative": vector(-42.76, -36.86) * mm, "endDerivative": vector(-68.1, -24.19) * mm});
            skFitSpline(sketch, "E129", {"points": [v(82.23, 47.22) * mm, v(79.87, 45.37) * mm, v(77.94, 44.02) * mm, v(75.93, 42.98) * mm, v(74.12, 42.17) * mm, v(72.04, 41.75) * mm, v(70.23, 41.83) * mm, v(67.88, 42.48) * mm, v(65.84, 43.44) * mm, v(63.53, 44.95) * mm, v(61.14, 46.76) * mm, v(58.52, 48.88) * mm, v(55.82, 51.15) * mm, v(53.2, 53.28) * mm, v(51.35, 54.57) * mm, v(49.57, 55.64) * mm, v(47.43, 56.55) * mm, v(46.13, 56.9) * mm, v(44.8, 57.1) * mm, v(42.67, 56.97) * mm, v(40.4, 56.26) * mm, v(37.94, 54.93) * mm, v(35.15, 52.93) * mm, v(33.18, 51.23) * mm, v(30.9, 49.26) * mm, v(28.37, 47.1) * mm, v(26.17, 45.28) * mm, v(24.35, 43.95) * mm, v(22.63, 42.84) * mm, v(20.72, 41.97) * mm, v(19.23, 41.55) * mm], "startDerivative": vector(-65.6, -51.95) * mm, "endDerivative": vector(-54.28, -13.22) * mm});
            skFitSpline(sketch, "E130", {"points": [v(82.23, 44.96) * mm, v(81.02, 43.96) * mm, v(79.3, 42.72) * mm, v(77.49, 41.55) * mm, v(75.59, 40.5) * mm, v(73.87, 39.85) * mm, v(71.99, 39.53) * mm, v(70.07, 39.56) * mm, v(67.67, 40.3) * mm, v(64.57, 42.01) * mm, v(61.62, 44.02) * mm, v(59.28, 45.99) * mm, v(56.68, 48.13) * mm, v(54.87, 49.64) * mm, v(52.98, 51.1) * mm, v(51.4, 52.24) * mm, v(49.8, 53.26) * mm, v(48.07, 54.03) * mm, v(46.3, 54.6) * mm, v(43.96, 54.86) * mm, v(41.6, 54.47) * mm, v(38.8, 53.09) * mm, v(36.06, 51.24) * mm, v(33.36, 49.16) * mm, v(31.63, 47.57) * mm, v(28.46, 44.96) * mm, v(26.75, 43.39) * mm, v(24.95, 42.1) * mm, v(23.14, 40.96) * mm, v(21.36, 40.03) * mm, v(19.23, 39.21) * mm], "startDerivative": vector(-42.76, -36.86) * mm, "endDerivative": vector(-68.1, -24.19) * mm});
            skFitSpline(sketch, "E131", {"points": [v(82.23, 43.7) * mm, v(79.87, 41.84) * mm, v(77.94, 40.5) * mm, v(75.93, 39.45) * mm, v(74.12, 38.64) * mm, v(72.04, 38.22) * mm, v(70.23, 38.3) * mm, v(67.88, 38.95) * mm, v(65.84, 39.91) * mm, v(63.53, 41.42) * mm, v(61.14, 43.23) * mm, v(58.52, 45.35) * mm, v(55.82, 47.62) * mm, v(53.2, 49.74) * mm, v(51.35, 51.04) * mm, v(49.57, 52.11) * mm, v(47.43, 53.02) * mm, v(46.13, 53.37) * mm, v(44.8, 53.57) * mm, v(42.67, 53.44) * mm, v(40.4, 52.73) * mm, v(37.94, 51.4) * mm, v(35.15, 49.4) * mm, v(33.18, 47.7) * mm, v(30.9, 45.73) * mm, v(28.37, 43.58) * mm, v(26.17, 41.75) * mm, v(24.35, 40.42) * mm, v(22.63, 39.31) * mm, v(20.72, 38.44) * mm, v(19.23, 38.02) * mm], "startDerivative": vector(-65.6, -51.95) * mm, "endDerivative": vector(-54.28, -13.22) * mm});
            skFitSpline(sketch, "E132", {"points": [v(82.23, 41.43) * mm, v(81.02, 40.42) * mm, v(79.3, 39.19) * mm, v(77.49, 38.02) * mm, v(75.59, 36.96) * mm, v(73.87, 36.32) * mm, v(71.99, 36) * mm, v(70.07, 36.03) * mm, v(67.67, 36.76) * mm, v(64.57, 38.48) * mm, v(61.62, 40.5) * mm, v(59.28, 42.46) * mm, v(56.68, 44.6) * mm, v(54.87, 46.1) * mm, v(52.98, 47.57) * mm, v(51.4, 48.7) * mm, v(49.8, 49.73) * mm, v(48.07, 50.5) * mm, v(46.3, 51.08) * mm, v(43.96, 51.33) * mm, v(41.6, 50.94) * mm, v(38.8, 49.56) * mm, v(36.06, 47.7) * mm, v(33.36, 45.63) * mm, v(31.63, 44.04) * mm, v(28.46, 41.43) * mm, v(26.75, 39.86) * mm, v(24.95, 38.58) * mm, v(23.14, 37.43) * mm, v(21.36, 36.5) * mm, v(19.23, 35.68) * mm], "startDerivative": vector(-42.76, -36.86) * mm, "endDerivative": vector(-68.1, -24.19) * mm});
            skFitSpline(sketch, "E133", {"points": [v(82.23, 39.93) * mm, v(79.87, 38.08) * mm, v(77.94, 36.73) * mm, v(75.93, 35.69) * mm, v(74.12, 34.88) * mm, v(72.04, 34.46) * mm, v(70.23, 34.53) * mm, v(67.88, 35.19) * mm, v(65.84, 36.15) * mm, v(63.53, 37.65) * mm, v(61.14, 39.47) * mm, v(58.52, 41.58) * mm, v(55.82, 43.86) * mm, v(53.2, 45.98) * mm, v(51.35, 47.28) * mm, v(49.57, 48.35) * mm, v(47.43, 49.25) * mm, v(46.13, 49.61) * mm, v(44.8, 49.8) * mm, v(42.67, 49.68) * mm, v(40.4, 48.96) * mm, v(37.94, 47.63) * mm, v(35.15, 45.64) * mm, v(33.18, 43.94) * mm, v(30.9, 41.97) * mm, v(28.37, 39.82) * mm, v(26.17, 37.98) * mm, v(24.35, 36.65) * mm, v(22.63, 35.55) * mm, v(20.72, 34.68) * mm, v(19.23, 34.26) * mm], "startDerivative": vector(-65.6, -51.95) * mm, "endDerivative": vector(-54.28, -13.22) * mm});
            skFitSpline(sketch, "E134", {"points": [v(82.23, 37.67) * mm, v(81.02, 36.66) * mm, v(79.3, 35.43) * mm, v(77.49, 34.26) * mm, v(75.59, 33.2) * mm, v(73.87, 32.56) * mm, v(71.99, 32.24) * mm, v(70.07, 32.27) * mm, v(67.67, 33) * mm, v(64.57, 34.72) * mm, v(61.62, 36.73) * mm, v(59.28, 38.7) * mm, v(56.68, 40.84) * mm, v(54.87, 42.34) * mm, v(52.98, 43.8) * mm, v(51.4, 44.95) * mm, v(49.8, 45.97) * mm, v(48.07, 46.74) * mm, v(46.3, 47.32) * mm, v(43.96, 47.57) * mm, v(41.6, 47.18) * mm, v(38.8, 45.8) * mm, v(36.06, 43.94) * mm, v(33.36, 41.86) * mm, v(31.63, 40.28) * mm, v(28.46, 37.67) * mm, v(26.75, 36.1) * mm, v(24.95, 34.81) * mm, v(23.14, 33.66) * mm, v(21.36, 32.74) * mm, v(19.23, 31.92) * mm], "startDerivative": vector(-42.76, -36.86) * mm, "endDerivative": vector(-68.1, -24.19) * mm});
            skFitSpline(sketch, "E135", {"points": [v(82.23, 36.12) * mm, v(79.87, 34.27) * mm, v(77.94, 32.92) * mm, v(75.93, 31.88) * mm, v(74.12, 31.07) * mm, v(72.04, 30.65) * mm, v(70.23, 30.72) * mm, v(67.88, 31.38) * mm, v(65.84, 32.34) * mm, v(63.53, 33.84) * mm, v(61.14, 35.66) * mm, v(58.52, 37.77) * mm, v(55.82, 40.05) * mm, v(53.2, 42.17) * mm, v(51.35, 43.47) * mm, v(49.57, 44.54) * mm, v(47.43, 45.44) * mm, v(46.13, 45.8) * mm, v(44.8, 46) * mm, v(42.67, 45.87) * mm, v(40.4, 45.15) * mm, v(37.94, 43.82) * mm, v(35.15, 41.83) * mm, v(33.18, 40.13) * mm, v(30.9, 38.16) * mm, v(28.37, 36) * mm, v(26.17, 34.17) * mm, v(24.35, 32.84) * mm, v(22.63, 31.74) * mm, v(20.72, 30.87) * mm, v(19.23, 30.45) * mm], "startDerivative": vector(-65.6, -51.95) * mm, "endDerivative": vector(-54.28, -13.22) * mm});
            skFitSpline(sketch, "E136", {"points": [v(82.23, 33.86) * mm, v(81.02, 32.85) * mm, v(79.3, 31.62) * mm, v(77.49, 30.45) * mm, v(75.59, 29.4) * mm, v(73.87, 28.75) * mm, v(71.99, 28.43) * mm, v(70.07, 28.46) * mm, v(67.67, 29.2) * mm, v(64.57, 30.9) * mm, v(61.62, 32.92) * mm, v(59.28, 34.89) * mm, v(56.68, 37.03) * mm, v(54.87, 38.53) * mm, v(52.98, 40) * mm, v(51.4, 41.14) * mm, v(49.8, 42.16) * mm, v(48.07, 42.93) * mm, v(46.3, 43.5) * mm, v(43.96, 43.76) * mm, v(41.6, 43.37) * mm, v(38.8, 41.98) * mm, v(36.06, 40.13) * mm, v(33.36, 38.05) * mm, v(31.63, 36.47) * mm, v(28.46, 33.86) * mm, v(26.75, 32.28) * mm, v(24.95, 31) * mm, v(23.14, 29.85) * mm, v(21.36, 28.93) * mm, v(19.23, 28.1) * mm], "startDerivative": vector(-42.76, -36.86) * mm, "endDerivative": vector(-68.1, -24.19) * mm});
            skFitSpline(sketch, "E137", {"points": [v(82.23, 32.36) * mm, v(79.87, 30.5) * mm, v(77.94, 29.16) * mm, v(75.93, 28.12) * mm, v(74.12, 27.3) * mm, v(72.04, 26.89) * mm, v(70.23, 26.96) * mm, v(67.88, 27.62) * mm, v(65.84, 28.58) * mm, v(63.53, 30.08) * mm, v(61.14, 31.9) * mm, v(58.52, 34.02) * mm, v(55.82, 36.29) * mm, v(53.2, 38.41) * mm, v(51.35, 39.7) * mm, v(49.57, 40.78) * mm, v(47.43, 41.69) * mm, v(46.13, 42.04) * mm, v(44.8, 42.24) * mm, v(42.67, 42.1) * mm, v(40.4, 41.4) * mm, v(37.94, 40.07) * mm, v(35.15, 38.07) * mm, v(33.18, 36.37) * mm, v(30.9, 34.4) * mm, v(28.37, 32.25) * mm, v(26.17, 30.41) * mm, v(24.35, 29.08) * mm, v(22.63, 27.98) * mm, v(20.72, 27.1) * mm, v(19.23, 26.69) * mm], "startDerivative": vector(-65.6, -51.95) * mm, "endDerivative": vector(-54.28, -13.22) * mm});
            skFitSpline(sketch, "E138", {"points": [v(82.23, 30.1) * mm, v(81.02, 29.1) * mm, v(79.3, 27.86) * mm, v(77.49, 26.69) * mm, v(75.59, 25.63) * mm, v(73.87, 25) * mm, v(71.99, 24.67) * mm, v(70.07, 24.7) * mm, v(67.67, 25.43) * mm, v(64.57, 27.15) * mm, v(61.62, 29.16) * mm, v(59.28, 31.13) * mm, v(56.68, 33.27) * mm, v(54.87, 34.77) * mm, v(52.98, 36.24) * mm, v(51.4, 37.38) * mm, v(49.8, 38.4) * mm, v(48.07, 39.17) * mm, v(46.3, 39.75) * mm, v(43.96, 40) * mm, v(41.6, 39.61) * mm, v(38.8, 38.22) * mm, v(36.06, 36.37) * mm, v(33.36, 34.3) * mm, v(31.63, 32.71) * mm, v(28.46, 30.1) * mm, v(26.75, 28.53) * mm, v(24.95, 27.24) * mm, v(23.14, 26.1) * mm, v(21.36, 25.17) * mm, v(19.23, 24.35) * mm], "startDerivative": vector(-42.76, -36.86) * mm, "endDerivative": vector(-68.1, -24.19) * mm});
            skFitSpline(sketch, "E139", {"points": [v(82.23, 28.75) * mm, v(79.87, 26.9) * mm, v(77.94, 25.55) * mm, v(75.93, 24.51) * mm, v(74.12, 23.7) * mm, v(72.04, 23.28) * mm, v(70.23, 23.35) * mm, v(67.88, 24) * mm, v(65.84, 24.97) * mm, v(63.53, 26.48) * mm, v(61.14, 28.29) * mm, v(58.52, 30.4) * mm, v(55.82, 32.68) * mm, v(53.2, 34.8) * mm, v(51.35, 36.1) * mm, v(49.57, 37.17) * mm, v(47.43, 38.08) * mm, v(46.13, 38.43) * mm, v(44.8, 38.63) * mm, v(42.67, 38.5) * mm, v(40.4, 37.79) * mm, v(37.94, 36.46) * mm, v(35.15, 34.46) * mm, v(33.18, 32.76) * mm, v(30.9, 30.8) * mm, v(28.37, 28.64) * mm, v(26.17, 26.8) * mm, v(24.35, 25.48) * mm, v(22.63, 24.37) * mm, v(20.72, 23.5) * mm, v(19.23, 23.08) * mm], "startDerivative": vector(-65.6, -51.95) * mm, "endDerivative": vector(-54.28, -13.22) * mm});
            skFitSpline(sketch, "E140", {"points": [v(82.23, 26.5) * mm, v(81.02, 25.48) * mm, v(79.3, 24.25) * mm, v(77.49, 23.08) * mm, v(75.59, 22.02) * mm, v(73.87, 21.38) * mm, v(71.99, 21.06) * mm, v(70.07, 21.09) * mm, v(67.67, 21.82) * mm, v(64.57, 23.54) * mm, v(61.62, 25.55) * mm, v(59.28, 27.52) * mm, v(56.68, 29.66) * mm, v(54.87, 31.17) * mm, v(52.98, 32.63) * mm, v(51.4, 33.77) * mm, v(49.8, 34.79) * mm, v(48.07, 35.56) * mm, v(46.3, 36.14) * mm, v(43.96, 36.39) * mm, v(41.6, 36) * mm, v(38.8, 34.62) * mm, v(36.06, 32.77) * mm, v(33.36, 30.68) * mm, v(31.63, 29.1) * mm, v(28.46, 26.5) * mm, v(26.75, 24.92) * mm, v(24.95, 23.64) * mm, v(23.14, 22.49) * mm, v(21.36, 21.56) * mm, v(19.23, 20.74) * mm], "startDerivative": vector(-42.76, -36.86) * mm, "endDerivative": vector(-68.1, -24.19) * mm});
            skFitSpline(sketch, "E141", {"points": [v(82.23, 25.27) * mm, v(79.87, 23.42) * mm, v(77.94, 22.07) * mm, v(75.93, 21.03) * mm, v(74.12, 20.22) * mm, v(72.04, 19.8) * mm, v(70.23, 19.88) * mm, v(67.88, 20.53) * mm, v(65.84, 21.5) * mm, v(63.53, 23) * mm, v(61.14, 24.8) * mm, v(58.52, 26.93) * mm, v(55.82, 29.2) * mm, v(53.2, 31.33) * mm, v(51.35, 32.62) * mm, v(49.57, 33.7) * mm, v(47.43, 34.6) * mm, v(46.13, 34.96) * mm, v(44.8, 35.15) * mm, v(42.67, 35.02) * mm, v(40.4, 34.3) * mm, v(37.94, 32.98) * mm, v(35.15, 30.98) * mm, v(33.18, 29.28) * mm, v(30.9, 27.31) * mm, v(28.37, 25.16) * mm, v(26.17, 23.33) * mm, v(24.35, 22) * mm, v(22.63, 20.9) * mm, v(20.72, 20.02) * mm, v(19.23, 19.6) * mm], "startDerivative": vector(-65.6, -51.95) * mm, "endDerivative": vector(-54.28, -13.22) * mm});
            skFitSpline(sketch, "E142", {"points": [v(82.23, 23.01) * mm, v(81.02, 22) * mm, v(79.3, 20.77) * mm, v(77.49, 19.6) * mm, v(75.59, 18.55) * mm, v(73.87, 17.9) * mm, v(71.99, 17.58) * mm, v(70.07, 17.6) * mm, v(67.67, 18.35) * mm, v(64.57, 20.06) * mm, v(61.62, 22.07) * mm, v(59.28, 24.04) * mm, v(56.68, 26.18) * mm, v(54.87, 27.69) * mm, v(52.98, 29.15) * mm, v(51.4, 30.29) * mm, v(49.8, 31.31) * mm, v(48.07, 32.08) * mm, v(46.3, 32.66) * mm, v(43.96, 32.91) * mm, v(41.6, 32.52) * mm, v(38.8, 31.14) * mm, v(36.06, 29.29) * mm, v(33.36, 27.2) * mm, v(31.63, 25.62) * mm, v(28.46, 23.01) * mm, v(26.75, 21.44) * mm, v(24.95, 20.16) * mm, v(23.14, 19) * mm, v(21.36, 18.08) * mm, v(19.23, 17.26) * mm], "startDerivative": vector(-42.76, -36.86) * mm, "endDerivative": vector(-68.1, -24.19) * mm});
            skFitSpline(sketch, "E143", {"points": [v(82.23, 21.72) * mm, v(79.87, 19.87) * mm, v(77.94, 18.52) * mm, v(75.93, 17.48) * mm, v(74.12, 16.67) * mm, v(72.04, 16.24) * mm, v(70.23, 16.32) * mm, v(67.88, 16.98) * mm, v(65.84, 17.94) * mm, v(63.53, 19.44) * mm, v(61.14, 21.25) * mm, v(58.52, 23.37) * mm, v(55.82, 25.65) * mm, v(53.2, 27.77) * mm, v(51.35, 29.07) * mm, v(49.57, 30.14) * mm, v(47.43, 31.04) * mm, v(46.13, 31.4) * mm, v(44.8, 31.6) * mm, v(42.67, 31.46) * mm, v(40.4, 30.75) * mm, v(37.94, 29.42) * mm, v(35.15, 27.42) * mm, v(33.18, 25.73) * mm, v(30.9, 23.76) * mm, v(28.37, 21.6) * mm, v(26.17, 19.77) * mm, v(24.35, 18.44) * mm, v(22.63, 17.34) * mm, v(20.72, 16.46) * mm, v(19.23, 16.04) * mm], "startDerivative": vector(-65.6, -51.95) * mm, "endDerivative": vector(-54.28, -13.22) * mm});
            skFitSpline(sketch, "E144", {"points": [v(82.23, 19.46) * mm, v(81.02, 18.45) * mm, v(79.3, 17.21) * mm, v(77.49, 16.04) * mm, v(75.59, 15) * mm, v(73.87, 14.35) * mm, v(71.99, 14.03) * mm, v(70.07, 14.05) * mm, v(67.67, 14.79) * mm, v(64.57, 16.5) * mm, v(61.62, 18.52) * mm, v(59.28, 20.48) * mm, v(56.68, 22.63) * mm, v(54.87, 24.13) * mm, v(52.98, 25.6) * mm, v(51.4, 26.73) * mm, v(49.8, 27.75) * mm, v(48.07, 28.52) * mm, v(46.3, 29.1) * mm, v(43.96, 29.35) * mm, v(41.6, 28.97) * mm, v(38.8, 27.58) * mm, v(36.06, 25.73) * mm, v(33.36, 23.65) * mm, v(31.63, 22.07) * mm, v(28.46, 19.46) * mm, v(26.75, 17.88) * mm, v(24.95, 16.6) * mm, v(23.14, 15.45) * mm, v(21.36, 14.53) * mm, v(19.23, 13.7) * mm], "startDerivative": vector(-42.76, -36.86) * mm, "endDerivative": vector(-68.1, -24.19) * mm});
            skFitSpline(sketch, "E145", {"points": [v(82.23, 18.09) * mm, v(79.87, 16.23) * mm, v(77.94, 14.88) * mm, v(75.93, 13.84) * mm, v(74.12, 13.03) * mm, v(72.04, 12.61) * mm, v(70.23, 12.69) * mm, v(67.88, 13.34) * mm, v(65.84, 14.3) * mm, v(63.53, 15.8) * mm, v(61.14, 17.62) * mm, v(58.52, 19.74) * mm, v(55.82, 22.01) * mm, v(53.2, 24.14) * mm, v(51.35, 25.43) * mm, v(49.57, 26.5) * mm, v(47.43, 27.41) * mm, v(46.13, 27.77) * mm, v(44.8, 27.96) * mm, v(42.67, 27.83) * mm, v(40.4, 27.12) * mm, v(37.94, 25.8) * mm, v(35.15, 23.8) * mm, v(33.18, 22.1) * mm, v(30.9, 20.13) * mm, v(28.37, 17.97) * mm, v(26.17, 16.14) * mm, v(24.35, 14.8) * mm, v(22.63, 13.7) * mm, v(20.72, 12.83) * mm, v(19.23, 12.41) * mm], "startDerivative": vector(-65.6, -51.95) * mm, "endDerivative": vector(-54.28, -13.22) * mm});
            skFitSpline(sketch, "E146", {"points": [v(82.23, 15.83) * mm, v(81.02, 14.82) * mm, v(79.3, 13.58) * mm, v(77.49, 12.41) * mm, v(75.59, 11.36) * mm, v(73.87, 10.72) * mm, v(71.99, 10.4) * mm, v(70.07, 10.42) * mm, v(67.67, 11.16) * mm, v(64.57, 12.87) * mm, v(61.62, 14.88) * mm, v(59.28, 16.85) * mm, v(56.68, 19) * mm, v(54.87, 20.5) * mm, v(52.98, 21.96) * mm, v(51.4, 23.1) * mm, v(49.8, 24.12) * mm, v(48.07, 24.9) * mm, v(46.3, 25.47) * mm, v(43.96, 25.72) * mm, v(41.6, 25.34) * mm, v(38.8, 23.95) * mm, v(36.06, 22.1) * mm, v(33.36, 20.02) * mm, v(31.63, 18.44) * mm, v(28.46, 15.83) * mm, v(26.75, 14.25) * mm, v(24.95, 12.97) * mm, v(23.14, 11.82) * mm, v(21.36, 10.9) * mm, v(19.23, 10.08) * mm], "startDerivative": vector(-42.76, -36.86) * mm, "endDerivative": vector(-68.1, -24.19) * mm});
            skFitSpline(sketch, "E147", {"points": [v(82.23, 14.33) * mm, v(79.87, 12.47) * mm, v(77.94, 11.13) * mm, v(75.93, 10.08) * mm, v(74.12, 9.28) * mm, v(72.04, 8.85) * mm, v(70.23, 8.93) * mm, v(67.88, 9.58) * mm, v(65.84, 10.55) * mm, v(63.53, 12.05) * mm, v(61.14, 13.86) * mm, v(58.52, 15.98) * mm, v(55.82, 18.25) * mm, v(53.2, 20.38) * mm, v(51.35, 21.67) * mm, v(49.57, 22.74) * mm, v(47.43, 23.65) * mm, v(46.13, 24) * mm, v(44.8, 24.2) * mm, v(42.67, 24.07) * mm, v(40.4, 23.36) * mm, v(37.94, 22.03) * mm, v(35.15, 20.03) * mm, v(33.18, 18.34) * mm, v(30.9, 16.37) * mm, v(28.37, 14.21) * mm, v(26.17, 12.38) * mm, v(24.35, 11.05) * mm, v(22.63, 9.95) * mm, v(20.72, 9.07) * mm, v(19.23, 8.65) * mm], "startDerivative": vector(-65.6, -51.95) * mm, "endDerivative": vector(-54.28, -13.22) * mm});
            skFitSpline(sketch, "E148", {"points": [v(82.23, 12.07) * mm, v(81.02, 11.06) * mm, v(79.3, 9.82) * mm, v(77.49, 8.65) * mm, v(75.59, 7.6) * mm, v(73.87, 6.96) * mm, v(71.99, 6.64) * mm, v(70.07, 6.66) * mm, v(67.67, 7.4) * mm, v(64.57, 9.11) * mm, v(61.62, 11.13) * mm, v(59.28, 13.1) * mm, v(56.68, 15.24) * mm, v(54.87, 16.74) * mm, v(52.98, 18.2) * mm, v(51.4, 19.34) * mm, v(49.8, 20.36) * mm, v(48.07, 21.13) * mm, v(46.3, 21.71) * mm, v(43.96, 21.96) * mm, v(41.6, 21.58) * mm, v(38.8, 20.19) * mm, v(36.06, 18.34) * mm, v(33.36, 16.26) * mm, v(31.63, 14.68) * mm, v(28.46, 12.07) * mm, v(26.75, 10.5) * mm, v(24.95, 9.21) * mm, v(23.14, 8.06) * mm, v(21.36, 7.13) * mm, v(19.23, 6.32) * mm], "startDerivative": vector(-42.76, -36.86) * mm, "endDerivative": vector(-68.1, -24.19) * mm});
            skFitSpline(sketch, "E149", {"points": [v(82.23, 10.64) * mm, v(79.87, 8.8) * mm, v(77.94, 7.44) * mm, v(75.93, 6.4) * mm, v(74.12, 5.6) * mm, v(72.04, 5.17) * mm, v(70.23, 5.25) * mm, v(67.88, 5.9) * mm, v(65.84, 6.86) * mm, v(63.53, 8.37) * mm, v(61.14, 10.18) * mm, v(58.52, 12.3) * mm, v(55.82, 14.57) * mm, v(53.2, 16.7) * mm, v(51.35, 18) * mm, v(49.57, 19.06) * mm, v(47.43, 19.97) * mm, v(46.13, 20.32) * mm, v(44.8, 20.52) * mm, v(42.67, 20.39) * mm, v(40.4, 19.68) * mm, v(37.94, 18.35) * mm, v(35.15, 16.35) * mm, v(33.18, 14.65) * mm, v(30.9, 12.68) * mm, v(28.37, 10.53) * mm, v(26.17, 8.7) * mm, v(24.35, 7.37) * mm, v(22.63, 6.26) * mm, v(20.72, 5.39) * mm, v(19.23, 4.97) * mm], "startDerivative": vector(-65.6, -51.95) * mm, "endDerivative": vector(-54.28, -13.22) * mm});
            skFitSpline(sketch, "E150", {"points": [v(82.23, 8.38) * mm, v(81.02, 7.38) * mm, v(79.3, 6.14) * mm, v(77.49, 4.97) * mm, v(75.59, 3.92) * mm, v(73.87, 3.27) * mm, v(71.99, 2.95) * mm, v(70.07, 2.98) * mm, v(67.67, 3.71) * mm, v(64.57, 5.43) * mm, v(61.62, 7.44) * mm, v(59.28, 9.4) * mm, v(56.68, 11.55) * mm, v(54.87, 13.06) * mm, v(52.98, 14.52) * mm, v(51.4, 15.66) * mm, v(49.8, 16.68) * mm, v(48.07, 17.45) * mm, v(46.3, 18.03) * mm, v(43.96, 18.28) * mm, v(41.6, 17.9) * mm, v(38.8, 16.5) * mm, v(36.06, 14.66) * mm, v(33.36, 12.58) * mm, v(31.63, 11) * mm, v(28.46, 8.38) * mm, v(26.75, 6.8) * mm, v(24.95, 5.53) * mm, v(23.14, 4.38) * mm, v(21.36, 3.45) * mm, v(19.23, 2.63) * mm], "startDerivative": vector(-42.76, -36.86) * mm, "endDerivative": vector(-68.1, -24.19) * mm});
            skFitSpline(sketch, "E151", {"points": [v(82.23, 6.86) * mm, v(79.87, 5) * mm, v(77.94, 3.66) * mm, v(75.93, 2.62) * mm, v(74.12, 1.8) * mm, v(72.04, 1.38) * mm, v(70.23, 1.46) * mm, v(67.88, 2.12) * mm, v(65.84, 3.08) * mm, v(63.53, 4.58) * mm, v(61.14, 6.4) * mm, v(58.52, 8.51) * mm, v(55.82, 10.79) * mm, v(53.2, 12.91) * mm, v(51.35, 14.2) * mm, v(49.57, 15.28) * mm, v(47.43, 16.18) * mm, v(46.13, 16.54) * mm, v(44.8, 16.73) * mm, v(42.67, 16.6) * mm, v(40.4, 15.9) * mm, v(37.94, 14.56) * mm, v(35.15, 12.57) * mm, v(33.18, 10.87) * mm, v(30.9, 8.9) * mm, v(28.37, 6.75) * mm, v(26.17, 4.91) * mm, v(24.35, 3.58) * mm, v(22.63, 2.48) * mm, v(20.72, 1.6) * mm, v(19.23, 1.18) * mm], "startDerivative": vector(-65.6, -51.95) * mm, "endDerivative": vector(-54.28, -13.22) * mm});
            skFitSpline(sketch, "E152", {"points": [v(82.23, 4.6) * mm, v(81.02, 3.6) * mm, v(79.3, 2.35) * mm, v(77.49, 1.19) * mm, v(75.59, 0.13) * mm, v(73.87, -0.51) * mm, v(71.99, -0.83) * mm, v(70.07, -0.8) * mm, v(67.67, -0.07) * mm, v(64.57, 1.65) * mm, v(61.62, 3.66) * mm, v(59.28, 5.63) * mm, v(56.68, 7.77) * mm, v(54.87, 9.27) * mm, v(52.98, 10.74) * mm, v(51.4, 11.87) * mm, v(49.8, 12.9) * mm, v(48.07, 13.67) * mm, v(46.3, 14.24) * mm, v(43.96, 14.5) * mm, v(41.6, 14.1) * mm, v(38.8, 12.72) * mm, v(36.06, 10.87) * mm, v(33.36, 8.8) * mm, v(31.63, 7.2) * mm, v(28.46, 4.6) * mm, v(26.75, 3.02) * mm, v(24.95, 1.74) * mm, v(23.14, 0.6) * mm, v(21.36, -0.33) * mm, v(19.23, -1.15) * mm], "startDerivative": vector(-42.76, -36.86) * mm, "endDerivative": vector(-68.1, -24.19) * mm});
            skFitSpline(sketch, "E153", {"points": [v(82.23, 3.23) * mm, v(79.87, 1.37) * mm, v(77.94, 0.03) * mm, v(75.93, -1.02) * mm, v(74.12, -1.82) * mm, v(72.04, -2.25) * mm, v(70.23, -2.17) * mm, v(67.88, -1.52) * mm, v(65.84, -0.55) * mm, v(63.53, 0.95) * mm, v(61.14, 2.76) * mm, v(58.52, 4.88) * mm, v(55.82, 7.15) * mm, v(53.2, 9.28) * mm, v(51.35, 10.57) * mm, v(49.57, 11.64) * mm, v(47.43, 12.55) * mm, v(46.13, 12.9) * mm, v(44.8, 13.1) * mm, v(42.67, 12.97) * mm, v(40.4, 12.26) * mm, v(37.94, 10.93) * mm, v(35.15, 8.93) * mm, v(33.18, 7.24) * mm, v(30.9, 5.27) * mm, v(28.37, 3.11) * mm, v(26.17, 1.28) * mm, v(24.35, -0.05) * mm, v(22.63, -1.15) * mm, v(20.72, -2.03) * mm, v(19.23, -2.45) * mm], "startDerivative": vector(-65.6, -51.95) * mm, "endDerivative": vector(-54.28, -13.22) * mm});
            skFitSpline(sketch, "E154", {"points": [v(82.23, 0.97) * mm, v(81.02, -0.04) * mm, v(79.3, -1.28) * mm, v(77.49, -2.45) * mm, v(75.59, -3.5) * mm, v(73.87, -4.14) * mm, v(71.99, -4.46) * mm, v(70.07, -4.44) * mm, v(67.67, -3.7) * mm, v(64.57, -1.99) * mm, v(61.62, 0.03) * mm, v(59.28, 2) * mm, v(56.68, 4.14) * mm, v(54.87, 5.64) * mm, v(52.98, 7.1) * mm, v(51.4, 8.24) * mm, v(49.8, 9.26) * mm, v(48.07, 10.03) * mm, v(46.3, 10.61) * mm, v(43.96, 10.86) * mm, v(41.6, 10.48) * mm, v(38.8, 9.1) * mm, v(36.06, 7.24) * mm, v(33.36, 5.16) * mm, v(31.63, 3.58) * mm, v(28.46, 0.97) * mm, v(26.75, -0.6) * mm, v(24.95, -1.89) * mm, v(23.14, -3.04) * mm, v(21.36, -3.97) * mm, v(19.23, -4.78) * mm], "startDerivative": vector(-42.76, -36.86) * mm, "endDerivative": vector(-68.1, -24.19) * mm});
            skFitSpline(sketch, "E155", {"points": [v(82.23, -0.25) * mm, v(79.87, -2.1) * mm, v(77.94, -3.45) * mm, v(75.93, -4.5) * mm, v(74.12, -5.3) * mm, v(72.04, -5.73) * mm, v(70.23, -5.65) * mm, v(67.88, -5) * mm, v(65.84, -4.03) * mm, v(63.53, -2.53) * mm, v(61.14, -0.72) * mm, v(58.52, 1.4) * mm, v(55.82, 3.67) * mm, v(53.2, 5.8) * mm, v(51.35, 7.1) * mm, v(49.57, 8.16) * mm, v(47.43, 9.07) * mm, v(46.13, 9.43) * mm, v(44.8, 9.62) * mm, v(42.67, 9.5) * mm, v(40.4, 8.78) * mm, v(37.94, 7.45) * mm, v(35.15, 5.45) * mm, v(33.18, 3.76) * mm, v(30.9, 1.79) * mm, v(28.37, -0.37) * mm, v(26.17, -2.2) * mm, v(24.35, -3.53) * mm, v(22.63, -4.63) * mm, v(20.72, -5.5) * mm, v(19.23, -5.93) * mm], "startDerivative": vector(-65.6, -51.95) * mm, "endDerivative": vector(-54.28, -13.22) * mm});
            skFitSpline(sketch, "E156", {"points": [v(82.23, -2.51) * mm, v(81.02, -3.52) * mm, v(79.3, -4.76) * mm, v(77.49, -5.93) * mm, v(75.59, -6.98) * mm, v(73.87, -7.62) * mm, v(71.99, -7.94) * mm, v(70.07, -7.92) * mm, v(67.67, -7.18) * mm, v(64.57, -5.47) * mm, v(61.62, -3.45) * mm, v(59.28, -1.49) * mm, v(56.68, 0.66) * mm, v(54.87, 2.16) * mm, v(52.98, 3.62) * mm, v(51.4, 4.76) * mm, v(49.8, 5.78) * mm, v(48.07, 6.55) * mm, v(46.3, 7.13) * mm, v(43.96, 7.38) * mm, v(41.6, 7) * mm, v(38.8, 5.61) * mm, v(36.06, 3.76) * mm, v(33.36, 1.68) * mm, v(31.63, 0.1) * mm, v(28.46, -2.51) * mm, v(26.75, -4.09) * mm, v(24.95, -5.37) * mm, v(23.14, -6.52) * mm, v(21.36, -7.45) * mm, v(19.23, -8.26) * mm], "startDerivative": vector(-42.76, -36.86) * mm, "endDerivative": vector(-68.1, -24.19) * mm});
            skFitSpline(sketch, "E157", {"points": [v(82.23, -6.4) * mm, v(81.02, -7.38) * mm, v(79.3, -8.62) * mm, v(77.49, -9.79) * mm, v(75.59, -10.84) * mm, v(73.87, -11.48) * mm, v(71.99, -11.8) * mm, v(70.07, -11.78) * mm, v(67.67, -11.04) * mm, v(64.57, -9.33) * mm, v(61.62, -7.32) * mm, v(59.28, -5.35) * mm, v(56.68, -3.2) * mm, v(54.87, -1.7) * mm, v(52.98, -0.24) * mm, v(51.4, 0.9) * mm, v(49.8, 1.92) * mm, v(48.07, 2.7) * mm, v(46.3, 3.27) * mm, v(43.96, 3.52) * mm, v(41.6, 3.14) * mm, v(38.8, 1.75) * mm, v(36.06, -0.1) * mm, v(33.36, -2.18) * mm, v(31.63, -3.76) * mm, v(28.46, -6.4) * mm, v(26.75, -7.95) * mm, v(24.95, -9.23) * mm, v(23.14, -10.38) * mm, v(21.36, -11.3) * mm, v(19.23, -12.12) * mm], "startDerivative": vector(-42.76, -36.86) * mm, "endDerivative": vector(-68.1, -24.19) * mm});
            skFitSpline(sketch, "E158", {"points": [v(82.23, -7.44) * mm, v(79.87, -9.3) * mm, v(77.94, -10.64) * mm, v(75.93, -11.68) * mm, v(74.12, -12.5) * mm, v(72.04, -12.92) * mm, v(70.23, -12.84) * mm, v(67.88, -12.18) * mm, v(65.84, -11.22) * mm, v(63.53, -9.72) * mm, v(61.14, -7.9) * mm, v(58.52, -5.79) * mm, v(55.82, -3.51) * mm, v(53.2, -1.39) * mm, v(51.35, -0.1) * mm, v(49.57, 0.98) * mm, v(47.43, 1.88) * mm, v(46.13, 2.24) * mm, v(44.8, 2.43) * mm, v(42.67, 2.3) * mm, v(40.4, 1.6) * mm, v(37.94, 0.26) * mm, v(35.15, -1.74) * mm, v(33.18, -3.43) * mm, v(30.9, -5.4) * mm, v(28.37, -7.56) * mm, v(26.17, -9.39) * mm, v(24.35, -10.72) * mm, v(22.63, -11.82) * mm, v(20.72, -12.7) * mm, v(19.23, -13.12) * mm], "startDerivative": vector(-65.6, -51.95) * mm, "endDerivative": vector(-54.28, -13.22) * mm});
            skFitSpline(sketch, "E159", {"points": [v(82.23, -9.7) * mm, v(81.02, -10.7) * mm, v(79.3, -11.95) * mm, v(77.49, -13.12) * mm, v(75.59, -14.17) * mm, v(73.87, -14.81) * mm, v(71.99, -15.13) * mm, v(70.07, -15.1) * mm, v(67.67, -14.37) * mm, v(64.57, -12.65) * mm, v(61.62, -10.64) * mm, v(59.28, -8.68) * mm, v(56.68, -6.53) * mm, v(54.87, -5.03) * mm, v(52.98, -3.56) * mm, v(51.4, -2.43) * mm, v(49.8, -1.4) * mm, v(48.07, -0.63) * mm, v(46.3, -0.06) * mm, v(43.96, 0.2) * mm, v(41.6, -0.2) * mm, v(38.8, -1.58) * mm, v(36.06, -3.43) * mm, v(33.36, -5.5) * mm, v(31.63, -7.1) * mm, v(28.46, -9.7) * mm, v(26.75, -11.28) * mm, v(24.95, -12.56) * mm, v(23.14, -13.7) * mm, v(21.36, -14.63) * mm, v(19.23, -15.45) * mm], "startDerivative": vector(-42.76, -36.86) * mm, "endDerivative": vector(-68.1, -24.19) * mm});
            skFitSpline(sketch, "E160", {"points": [v(82.23, -11.25) * mm, v(79.87, -13.1) * mm, v(77.94, -14.45) * mm, v(75.93, -15.5) * mm, v(74.12, -16.3) * mm, v(72.04, -16.73) * mm, v(70.23, -16.65) * mm, v(67.88, -16) * mm, v(65.84, -15.03) * mm, v(63.53, -13.53) * mm, v(61.14, -11.72) * mm, v(58.52, -9.6) * mm, v(55.82, -7.32) * mm, v(53.2, -5.2) * mm, v(51.35, -3.9) * mm, v(49.57, -2.83) * mm, v(47.43, -1.93) * mm, v(46.13, -1.57) * mm, v(44.8, -1.38) * mm, v(42.67, -1.5) * mm, v(40.4, -2.22) * mm, v(37.94, -3.55) * mm, v(35.15, -5.55) * mm, v(33.18, -7.24) * mm, v(30.9, -9.21) * mm, v(28.37, -11.37) * mm, v(26.17, -13.2) * mm, v(24.35, -14.53) * mm, v(22.63, -15.63) * mm, v(20.72, -16.5) * mm, v(19.23, -16.93) * mm], "startDerivative": vector(-65.6, -51.95) * mm, "endDerivative": vector(-54.28, -13.22) * mm});
            skFitSpline(sketch, "E161", {"points": [v(82.23, -13.51) * mm, v(81.02, -14.52) * mm, v(79.3, -15.76) * mm, v(77.49, -16.93) * mm, v(75.59, -17.98) * mm, v(73.87, -18.62) * mm, v(71.99, -18.94) * mm, v(70.07, -18.92) * mm, v(67.67, -18.18) * mm, v(64.57, -16.46) * mm, v(61.62, -14.45) * mm, v(59.28, -12.49) * mm, v(56.68, -10.34) * mm, v(54.87, -8.84) * mm, v(52.98, -7.37) * mm, v(51.4, -6.24) * mm, v(49.8, -5.22) * mm, v(48.07, -4.44) * mm, v(46.3, -3.87) * mm, v(43.96, -3.62) * mm, v(41.6, -4) * mm, v(38.8, -5.39) * mm, v(36.06, -7.24) * mm, v(33.36, -9.32) * mm, v(31.63, -10.9) * mm, v(28.46, -13.51) * mm, v(26.75, -15.09) * mm, v(24.95, -16.37) * mm, v(23.14, -17.52) * mm, v(21.36, -18.44) * mm, v(19.23, -19.26) * mm], "startDerivative": vector(-42.76, -36.86) * mm, "endDerivative": vector(-68.1, -24.19) * mm});
            skFitSpline(sketch, "E162", {"points": [v(82.23, -14.65) * mm, v(79.87, -16.48) * mm, v(77.94, -17.83) * mm, v(75.93, -18.87) * mm, v(74.12, -19.68) * mm, v(72.04, -20.1) * mm, v(70.23, -20.03) * mm, v(67.88, -19.37) * mm, v(65.84, -18.4) * mm, v(63.53, -16.9) * mm, v(61.14, -15.1) * mm, v(58.52, -12.98) * mm, v(55.82, -10.7) * mm, v(53.2, -8.58) * mm, v(51.35, -7.28) * mm, v(49.57, -6.21) * mm, v(47.43, -5.3) * mm, v(46.13, -4.95) * mm, v(44.8, -4.75) * mm, v(42.67, -4.88) * mm, v(40.4, -5.6) * mm, v(37.94, -6.93) * mm, v(35.15, -8.92) * mm, v(33.18, -10.62) * mm, v(30.9, -12.59) * mm, v(28.37, -14.74) * mm, v(26.17, -16.58) * mm, v(24.35, -17.9) * mm, v(22.63, -19) * mm, v(20.72, -19.88) * mm, v(19.23, -20.3) * mm], "startDerivative": vector(-65.6, -51.95) * mm, "endDerivative": vector(-54.28, -13.22) * mm});
            skLineSegment(sketch, "E163", {"start": v(19.23, 76.45) * mm, "end": v(79.9, 76.25) * mm});
            skFitSpline(sketch, "E164.trimOffspring", {"points": [v(82.23, 72.86) * mm, v(79.87, 71) * mm, v(77.94, 69.65) * mm, v(75.93, 68.61) * mm, v(74.12, 67.8) * mm, v(72.04, 67.38) * mm, v(70.23, 67.46) * mm, v(67.88, 68.11) * mm, v(65.84, 69.08) * mm, v(63.53, 70.58) * mm, v(61.14, 72.4) * mm, v(58.52, 74.51) * mm, v(55.82, 76.78) * mm, v(53.2, 78.9) * mm, v(51.35, 80.2) * mm, v(49.57, 81.27) * mm, v(47.43, 82.18) * mm, v(46.13, 82.54) * mm, v(44.8, 82.73) * mm, v(42.67, 82.6) * mm, v(40.4, 81.89) * mm, v(37.94, 80.56) * mm, v(35.15, 78.56) * mm, v(33.18, 76.87) * mm, v(30.9, 74.9) * mm, v(28.37, 72.74) * mm, v(26.17, 70.9) * mm, v(24.35, 69.58) * mm, v(22.63, 68.48) * mm, v(20.72, 67.6) * mm, v(19.23, 67.18) * mm], "startDerivative": vector(-65.6, -51.95) * mm, "endDerivative": vector(-54.28, -13.22) * mm});
            skPoint(sketch, "E165.10.internal.orphan", {"position": v(61.62, -17.83) * mm});
            skPoint(sketch, "E165.25.internal.orphan", {"position": v(28.46, -16.9) * mm});
            skPoint(sketch, "E165.30.internal.orphan", {"position": v(19.23, -22.64) * mm});
            skFitSpline(sketch, "E166.trimOffspring", {"points": [v(82.23, -4.13) * mm, v(79.87, -5.97) * mm, v(77.94, -7.32) * mm, v(75.93, -8.36) * mm, v(74.12, -9.17) * mm, v(72.04, -9.59) * mm, v(70.23, -9.51) * mm, v(67.88, -8.86) * mm, v(65.84, -7.9) * mm, v(63.53, -6.4) * mm, v(61.14, -4.58) * mm, v(58.52, -2.46) * mm, v(55.82, -0.19) * mm, v(53.2, 1.94) * mm, v(51.35, 3.23) * mm, v(49.57, 4.3) * mm, v(47.43, 5.21) * mm, v(46.13, 5.57) * mm, v(44.8, 5.76) * mm, v(42.67, 5.63) * mm, v(40.4, 4.92) * mm, v(37.94, 3.6) * mm, v(35.15, 1.6) * mm, v(33.18, -0.1) * mm, v(30.9, -2.07) * mm, v(28.37, -4.23) * mm, v(26.17, -6.06) * mm, v(24.35, -7.4) * mm, v(22.63, -8.5) * mm, v(20.72, -9.37) * mm, v(19.23, -9.79) * mm], "startDerivative": vector(-65.6, -51.95) * mm, "endDerivative": vector(-54.28, -13.22) * mm});
            skLineSegment(sketch, "E167", {"start": v(79.9, -5.45) * mm, "end": v(79.9, 83.12) * mm});
            skPoint(sketch, "E168.orphan", {"position": v(81.85, -18.04) * mm});
            skPoint(sketch, "E169.orphan", {"position": v(82.23, -5.83) * mm});
            skLineSegment(sketch, "E170", {"start": v(19.23, -5.55) * mm, "end": v(19.23, 76.45) * mm});
            skLineSegment(sketch, "E171", {"start": v(78.25, -5.45) * mm, "end": v(19.23, -5.55) * mm});
            skLineSegment(sketch, "E172", {"start": v(78.25, -5.45) * mm, "end": v(79.9, -5.45) * mm});
            skSolve(sketch);
        }
    });
